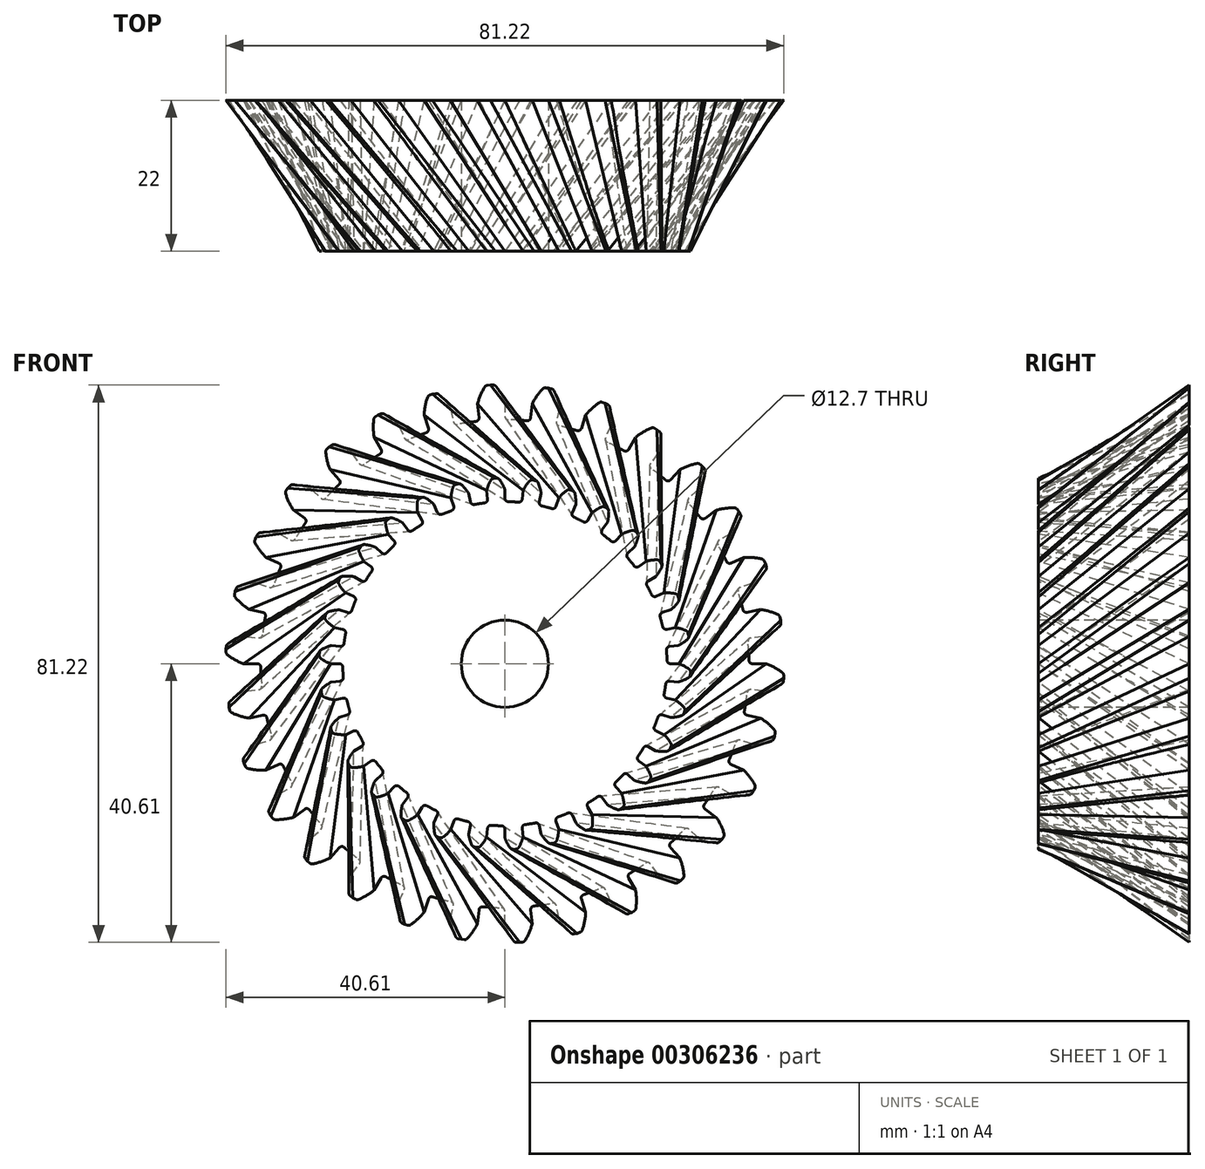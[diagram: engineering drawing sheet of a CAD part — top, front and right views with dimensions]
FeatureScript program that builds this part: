
annotation { "Feature Type Name" : "Feature", "Feature Type Description" : "" }
export const myFeature = defineFeature(function(context is Context, id is Id, definition is map)
    precondition{}
    {
        {
            var Q0;
            Q0=qCreatedBy(makeId("Front.planeOp"),FACE);
            var sketch = newSketch(context, id + "F0", { "sketchPlane" : qUnion([Q0])});
            skArc(sketch, "E0", {"start": v(-4.21, 35.3) * mm, "mid": v(-5.56, 35.12) * mm, "end": v(-6.9, 34.88) * mm});
            skLineSegment(sketch, "E1", {"start": v(0, 0) * mm, "end": v(-3.2, 60.87) * mm, "construction": true});
            skLineSegment(sketch, "E2", {"start": v(-1.69, 40.61) * mm, "end": v(-2.13, 40.61) * mm});
            skLineSegment(sketch, "E3", {"start": v(0, 38.1) * mm, "end": v(0, 36.06) * mm});
            skArc(sketch, "E4.trimOffspring", {"start": v(0, 38.1) * mm, "mid": v(-0.56, 39.3) * mm, "end": v(-1.28, 40.41) * mm});
            skLineSegment(sketch, "E5.MirrorCS", {"start": v(-2.57, 40.57) * mm, "end": v(-2.13, 40.61) * mm});
            skArc(sketch, "E6.MirrorCS", {"start": v(-3.98, 37.9) * mm, "mid": v(-3.55, 39.14) * mm, "end": v(-2.95, 40.32) * mm});
            skLineSegment(sketch, "E7.MirrorCS", {"start": v(-3.98, 37.9) * mm, "end": v(-3.77, 35.87) * mm});
            skPoint(sketch, "E8.orphan", {"position": v(0, 33.66) * mm});
            skPoint(sketch, "E9.orphan", {"position": v(-3.52, 33.47) * mm});
            skPoint(sketch, "E10.visualSharp", {"position": v(-2.81, 40.54) * mm});
            skArc(sketch, "E10.filletArc", {"start": v(-2.57, 40.57) * mm, "mid": v(-2.79, 40.5) * mm, "end": v(-2.95, 40.32) * mm});
            skPoint(sketch, "E11.visualSharp", {"position": v(-1.44, 40.61) * mm});
            skArc(sketch, "E11.filletArc", {"start": v(-1.28, 40.41) * mm, "mid": v(-1.46, 40.56) * mm, "end": v(-1.69, 40.61) * mm});
            skPoint(sketch, "E12.visualSharp", {"position": v(-3.72, 35.37) * mm});
            skArc(sketch, "E12.filletArc", {"start": v(-4.21, 35.3) * mm, "mid": v(-3.88, 35.5) * mm, "end": v(-3.77, 35.87) * mm});
            skPoint(sketch, "E13.visualSharp", {"position": v(0, 35.56) * mm});
            skArc(sketch, "E13.filletArc", {"start": v(0, 36.06) * mm, "mid": v(0.15, 35.7) * mm, "end": v(0.5, 35.56) * mm});
            skArc(sketch, "E14.1.0", {"start": v(-11.46, 33.66) * mm, "mid": v(-11.17, 33.91) * mm, "end": v(-11.14, 34.3) * mm});
            skLineSegment(sketch, "E14.1.1", {"start": v(-11.77, 36.24) * mm, "end": v(-11.14, 34.3) * mm});
            skArc(sketch, "E14.1.2", {"start": v(-11.77, 36.24) * mm, "mid": v(-11.61, 37.55) * mm, "end": v(-11.27, 38.83) * mm});
            skLineSegment(sketch, "E14.1.3", {"start": v(-10.95, 39.15) * mm, "end": v(-10.53, 39.28) * mm});
            skArc(sketch, "E14.1.4", {"start": v(-10.95, 39.15) * mm, "mid": v(-11.14, 39.03) * mm, "end": v(-11.27, 38.83) * mm});
            skLineSegment(sketch, "E14.1.5", {"start": v(-10.1, 39.38) * mm, "end": v(-10.53, 39.28) * mm});
            skArc(sketch, "E14.1.6", {"start": v(-9.66, 39.26) * mm, "mid": v(-9.86, 39.37) * mm, "end": v(-10.1, 39.38) * mm});
            skArc(sketch, "E14.1.7", {"start": v(-7.92, 37.27) * mm, "mid": v(-8.72, 38.33) * mm, "end": v(-9.66, 39.26) * mm});
            skLineSegment(sketch, "E14.1.8", {"start": v(-7.92, 37.27) * mm, "end": v(-7.5, 35.28) * mm});
            skArc(sketch, "E14.1.9", {"start": v(-7.5, 35.28) * mm, "mid": v(-7.28, 34.96) * mm, "end": v(-6.9, 34.88) * mm});
            skArc(sketch, "E14.2.0", {"start": v(-18.21, 30.54) * mm, "mid": v(-17.98, 30.85) * mm, "end": v(-18.03, 31.23) * mm});
            skLineSegment(sketch, "E14.2.1", {"start": v(-19.05, 33) * mm, "end": v(-18.03, 31.23) * mm});
            skArc(sketch, "E14.2.2", {"start": v(-19.05, 33) * mm, "mid": v(-19.16, 34.32) * mm, "end": v(-19.1, 35.64) * mm});
            skLineSegment(sketch, "E14.2.3", {"start": v(-18.85, 36.02) * mm, "end": v(-18.46, 36.24) * mm});
            skArc(sketch, "E14.2.4", {"start": v(-18.85, 36.02) * mm, "mid": v(-19.01, 35.86) * mm, "end": v(-19.1, 35.64) * mm});
            skLineSegment(sketch, "E14.2.5", {"start": v(-18.06, 36.42) * mm, "end": v(-18.46, 36.24) * mm});
            skArc(sketch, "E14.2.6", {"start": v(-17.6, 36.4) * mm, "mid": v(-17.83, 36.46) * mm, "end": v(-18.06, 36.42) * mm});
            skArc(sketch, "E14.2.7", {"start": v(-15.5, 34.8) * mm, "mid": v(-16.5, 35.68) * mm, "end": v(-17.6, 36.4) * mm});
            skLineSegment(sketch, "E14.2.8", {"start": v(-15.5, 34.8) * mm, "end": v(-14.67, 32.95) * mm});
            skArc(sketch, "E14.2.9", {"start": v(-14.67, 32.95) * mm, "mid": v(-14.4, 32.68) * mm, "end": v(-14, 32.69) * mm});
            skArc(sketch, "E14.3.0", {"start": v(-24.16, 26.09) * mm, "mid": v(-24, 26.44) * mm, "end": v(-24.13, 26.8) * mm});
            skLineSegment(sketch, "E14.3.1", {"start": v(-25.5, 28.31) * mm, "end": v(-24.13, 26.8) * mm});
            skArc(sketch, "E14.3.2", {"start": v(-25.5, 28.31) * mm, "mid": v(-25.88, 29.58) * mm, "end": v(-26.09, 30.9) * mm});
            skLineSegment(sketch, "E14.3.3", {"start": v(-25.92, 31.31) * mm, "end": v(-25.6, 31.6) * mm});
            skArc(sketch, "E14.3.4", {"start": v(-25.92, 31.31) * mm, "mid": v(-26.05, 31.12) * mm, "end": v(-26.09, 30.9) * mm});
            skLineSegment(sketch, "E14.3.5", {"start": v(-25.24, 31.87) * mm, "end": v(-25.6, 31.6) * mm});
            skArc(sketch, "E14.3.6", {"start": v(-24.8, 31.94) * mm, "mid": v(-25.02, 31.96) * mm, "end": v(-25.24, 31.87) * mm});
            skArc(sketch, "E14.3.7", {"start": v(-22.4, 30.82) * mm, "mid": v(-23.55, 31.47) * mm, "end": v(-24.8, 31.94) * mm});
            skLineSegment(sketch, "E14.3.8", {"start": v(-22.4, 30.82) * mm, "end": v(-21.2, 29.18) * mm});
            skArc(sketch, "E14.3.9", {"start": v(-21.2, 29.18) * mm, "mid": v(-20.87, 28.97) * mm, "end": v(-20.5, 29.06) * mm});
            skArc(sketch, "E14.4.0", {"start": v(-29.06, 20.5) * mm, "mid": v(-28.97, 20.87) * mm, "end": v(-29.18, 21.2) * mm});
            skLineSegment(sketch, "E14.4.1", {"start": v(-30.82, 22.4) * mm, "end": v(-29.18, 21.2) * mm});
            skArc(sketch, "E14.4.2", {"start": v(-30.82, 22.4) * mm, "mid": v(-31.47, 23.55) * mm, "end": v(-31.94, 24.8) * mm});
            skLineSegment(sketch, "E14.4.3", {"start": v(-31.87, 25.24) * mm, "end": v(-31.6, 25.6) * mm});
            skArc(sketch, "E14.4.4", {"start": v(-31.87, 25.24) * mm, "mid": v(-31.96, 25.02) * mm, "end": v(-31.94, 24.8) * mm});
            skLineSegment(sketch, "E14.4.5", {"start": v(-31.31, 25.92) * mm, "end": v(-31.6, 25.6) * mm});
            skArc(sketch, "E14.4.6", {"start": v(-30.9, 26.09) * mm, "mid": v(-31.12, 26.05) * mm, "end": v(-31.31, 25.92) * mm});
            skArc(sketch, "E14.4.7", {"start": v(-28.31, 25.5) * mm, "mid": v(-29.58, 25.88) * mm, "end": v(-30.9, 26.09) * mm});
            skLineSegment(sketch, "E14.4.8", {"start": v(-28.31, 25.5) * mm, "end": v(-26.8, 24.13) * mm});
            skArc(sketch, "E14.4.9", {"start": v(-26.8, 24.13) * mm, "mid": v(-26.44, 24) * mm, "end": v(-26.09, 24.16) * mm});
            skArc(sketch, "E14.5.0", {"start": v(-32.69, 14) * mm, "mid": v(-32.68, 14.4) * mm, "end": v(-32.95, 14.67) * mm});
            skLineSegment(sketch, "E14.5.1", {"start": v(-34.8, 15.5) * mm, "end": v(-32.95, 14.67) * mm});
            skArc(sketch, "E14.5.2", {"start": v(-34.8, 15.5) * mm, "mid": v(-35.68, 16.5) * mm, "end": v(-36.4, 17.6) * mm});
            skLineSegment(sketch, "E14.5.3", {"start": v(-36.42, 18.06) * mm, "end": v(-36.24, 18.46) * mm});
            skArc(sketch, "E14.5.4", {"start": v(-36.42, 18.06) * mm, "mid": v(-36.46, 17.83) * mm, "end": v(-36.4, 17.6) * mm});
            skLineSegment(sketch, "E14.5.5", {"start": v(-36.02, 18.85) * mm, "end": v(-36.24, 18.46) * mm});
            skArc(sketch, "E14.5.6", {"start": v(-35.64, 19.1) * mm, "mid": v(-35.86, 19.01) * mm, "end": v(-36.02, 18.85) * mm});
            skArc(sketch, "E14.5.7", {"start": v(-33, 19.05) * mm, "mid": v(-34.32, 19.16) * mm, "end": v(-35.64, 19.1) * mm});
            skLineSegment(sketch, "E14.5.8", {"start": v(-33, 19.05) * mm, "end": v(-31.23, 18.03) * mm});
            skArc(sketch, "E14.5.9", {"start": v(-31.23, 18.03) * mm, "mid": v(-30.85, 17.98) * mm, "end": v(-30.54, 18.21) * mm});
            skArc(sketch, "E14.6.0", {"start": v(-34.88, 6.9) * mm, "mid": v(-34.96, 7.28) * mm, "end": v(-35.28, 7.5) * mm});
            skLineSegment(sketch, "E14.6.1", {"start": v(-37.27, 7.92) * mm, "end": v(-35.28, 7.5) * mm});
            skArc(sketch, "E14.6.2", {"start": v(-37.27, 7.92) * mm, "mid": v(-38.33, 8.72) * mm, "end": v(-39.26, 9.66) * mm});
            skLineSegment(sketch, "E14.6.3", {"start": v(-39.38, 10.1) * mm, "end": v(-39.28, 10.53) * mm});
            skArc(sketch, "E14.6.4", {"start": v(-39.38, 10.1) * mm, "mid": v(-39.37, 9.86) * mm, "end": v(-39.26, 9.66) * mm});
            skLineSegment(sketch, "E14.6.5", {"start": v(-39.15, 10.95) * mm, "end": v(-39.28, 10.53) * mm});
            skArc(sketch, "E14.6.6", {"start": v(-38.83, 11.27) * mm, "mid": v(-39.03, 11.14) * mm, "end": v(-39.15, 10.95) * mm});
            skArc(sketch, "E14.6.7", {"start": v(-36.24, 11.77) * mm, "mid": v(-37.55, 11.61) * mm, "end": v(-38.83, 11.27) * mm});
            skLineSegment(sketch, "E14.6.8", {"start": v(-36.24, 11.77) * mm, "end": v(-34.3, 11.14) * mm});
            skArc(sketch, "E14.6.9", {"start": v(-34.3, 11.14) * mm, "mid": v(-33.91, 11.17) * mm, "end": v(-33.66, 11.46) * mm});
            skArc(sketch, "E14.7.0", {"start": v(-35.56, -0.5) * mm, "mid": v(-35.7, -0.15) * mm, "end": v(-36.06, 0) * mm});
            skLineSegment(sketch, "E14.7.1", {"start": v(-38.1, 0) * mm, "end": v(-36.06, 0) * mm});
            skArc(sketch, "E14.7.2", {"start": v(-38.1, 0) * mm, "mid": v(-39.3, 0.56) * mm, "end": v(-40.41, 1.28) * mm});
            skLineSegment(sketch, "E14.7.3", {"start": v(-40.61, 1.69) * mm, "end": v(-40.61, 2.13) * mm});
            skArc(sketch, "E14.7.4", {"start": v(-40.61, 1.69) * mm, "mid": v(-40.56, 1.46) * mm, "end": v(-40.41, 1.28) * mm});
            skLineSegment(sketch, "E14.7.5", {"start": v(-40.57, 2.57) * mm, "end": v(-40.61, 2.13) * mm});
            skArc(sketch, "E14.7.6", {"start": v(-40.32, 2.95) * mm, "mid": v(-40.5, 2.79) * mm, "end": v(-40.57, 2.57) * mm});
            skArc(sketch, "E14.7.7", {"start": v(-37.9, 3.98) * mm, "mid": v(-39.14, 3.55) * mm, "end": v(-40.32, 2.95) * mm});
            skLineSegment(sketch, "E14.7.8", {"start": v(-37.9, 3.98) * mm, "end": v(-35.87, 3.77) * mm});
            skArc(sketch, "E14.7.9", {"start": v(-35.87, 3.77) * mm, "mid": v(-35.5, 3.88) * mm, "end": v(-35.3, 4.21) * mm});
            skArc(sketch, "E14.8.0", {"start": v(-34.68, -7.88) * mm, "mid": v(-34.9, -7.57) * mm, "end": v(-35.28, -7.5) * mm});
            skLineSegment(sketch, "E14.8.1", {"start": v(-37.27, -7.92) * mm, "end": v(-35.28, -7.5) * mm});
            skArc(sketch, "E14.8.2", {"start": v(-37.27, -7.92) * mm, "mid": v(-38.56, -7.62) * mm, "end": v(-39.8, -7.15) * mm});
            skLineSegment(sketch, "E14.8.3", {"start": v(-40.08, -6.8) * mm, "end": v(-40.17, -6.36) * mm});
            skArc(sketch, "E14.8.4", {"start": v(-40.08, -6.8) * mm, "mid": v(-39.98, -7) * mm, "end": v(-39.8, -7.15) * mm});
            skLineSegment(sketch, "E14.8.5", {"start": v(-40.22, -5.92) * mm, "end": v(-40.17, -6.36) * mm});
            skArc(sketch, "E14.8.6", {"start": v(-40.06, -5.5) * mm, "mid": v(-40.19, -5.7) * mm, "end": v(-40.22, -5.92) * mm});
            skArc(sketch, "E14.8.7", {"start": v(-37.9, -3.98) * mm, "mid": v(-39.03, -4.67) * mm, "end": v(-40.06, -5.5) * mm});
            skLineSegment(sketch, "E14.8.8", {"start": v(-37.9, -3.98) * mm, "end": v(-35.87, -3.77) * mm});
            skArc(sketch, "E14.8.9", {"start": v(-35.87, -3.77) * mm, "mid": v(-35.53, -3.59) * mm, "end": v(-35.41, -3.22) * mm});
            skArc(sketch, "E14.9.0", {"start": v(-32.28, -14.92) * mm, "mid": v(-32.56, -14.66) * mm, "end": v(-32.95, -14.67) * mm});
            skLineSegment(sketch, "E14.9.1", {"start": v(-34.8, -15.5) * mm, "end": v(-32.95, -14.67) * mm});
            skArc(sketch, "E14.9.2", {"start": v(-34.8, -15.5) * mm, "mid": v(-36.13, -15.47) * mm, "end": v(-37.44, -15.27) * mm});
            skLineSegment(sketch, "E14.9.3", {"start": v(-37.79, -14.98) * mm, "end": v(-37.97, -14.57) * mm});
            skArc(sketch, "E14.9.4", {"start": v(-37.79, -14.98) * mm, "mid": v(-37.65, -15.16) * mm, "end": v(-37.44, -15.27) * mm});
            skLineSegment(sketch, "E14.9.5", {"start": v(-38.1, -14.16) * mm, "end": v(-37.97, -14.57) * mm});
            skArc(sketch, "E14.9.6", {"start": v(-38.04, -13.7) * mm, "mid": v(-38.12, -13.92) * mm, "end": v(-38.1, -14.16) * mm});
            skArc(sketch, "E14.9.7", {"start": v(-36.24, -11.77) * mm, "mid": v(-37.2, -12.68) * mm, "end": v(-38.04, -13.7) * mm});
            skLineSegment(sketch, "E14.9.8", {"start": v(-36.24, -11.77) * mm, "end": v(-34.3, -11.14) * mm});
            skArc(sketch, "E14.9.9", {"start": v(-34.3, -11.14) * mm, "mid": v(-34, -10.9) * mm, "end": v(-33.97, -10.51) * mm});
            skArc(sketch, "E14.10.0", {"start": v(-28.47, -21.3) * mm, "mid": v(-28.8, -21.1) * mm, "end": v(-29.18, -21.2) * mm});
            skLineSegment(sketch, "E14.10.1", {"start": v(-30.82, -22.4) * mm, "end": v(-29.18, -21.2) * mm});
            skArc(sketch, "E14.10.2", {"start": v(-30.82, -22.4) * mm, "mid": v(-32.12, -22.65) * mm, "end": v(-33.45, -22.72) * mm});
            skLineSegment(sketch, "E14.10.3", {"start": v(-33.85, -22.5) * mm, "end": v(-34.1, -22.15) * mm});
            skArc(sketch, "E14.10.4", {"start": v(-33.85, -22.5) * mm, "mid": v(-33.67, -22.66) * mm, "end": v(-33.45, -22.72) * mm});
            skLineSegment(sketch, "E14.10.5", {"start": v(-34.33, -21.77) * mm, "end": v(-34.1, -22.15) * mm});
            skArc(sketch, "E14.10.6", {"start": v(-34.36, -21.32) * mm, "mid": v(-34.4, -21.55) * mm, "end": v(-34.33, -21.77) * mm});
            skArc(sketch, "E14.10.7", {"start": v(-33, -19.05) * mm, "mid": v(-33.76, -20.14) * mm, "end": v(-34.36, -21.32) * mm});
            skLineSegment(sketch, "E14.10.8", {"start": v(-33, -19.05) * mm, "end": v(-31.23, -18.03) * mm});
            skArc(sketch, "E14.10.9", {"start": v(-31.23, -18.03) * mm, "mid": v(-31, -17.73) * mm, "end": v(-31.04, -17.34) * mm});
            skArc(sketch, "E14.11.0", {"start": v(-23.42, -26.76) * mm, "mid": v(-23.78, -26.63) * mm, "end": v(-24.13, -26.8) * mm});
            skLineSegment(sketch, "E14.11.1", {"start": v(-25.5, -28.31) * mm, "end": v(-24.13, -26.8) * mm});
            skArc(sketch, "E14.11.2", {"start": v(-25.5, -28.31) * mm, "mid": v(-26.71, -28.83) * mm, "end": v(-28, -29.17) * mm});
            skLineSegment(sketch, "E14.11.3", {"start": v(-28.43, -29.05) * mm, "end": v(-28.76, -28.76) * mm});
            skArc(sketch, "E14.11.4", {"start": v(-28.43, -29.05) * mm, "mid": v(-28.23, -29.16) * mm, "end": v(-28, -29.17) * mm});
            skLineSegment(sketch, "E14.11.5", {"start": v(-29.05, -28.43) * mm, "end": v(-28.76, -28.76) * mm});
            skArc(sketch, "E14.11.6", {"start": v(-29.17, -28) * mm, "mid": v(-29.16, -28.23) * mm, "end": v(-29.05, -28.43) * mm});
            skArc(sketch, "E14.11.7", {"start": v(-28.31, -25.5) * mm, "mid": v(-28.83, -26.71) * mm, "end": v(-29.17, -28) * mm});
            skLineSegment(sketch, "E14.11.8", {"start": v(-28.31, -25.5) * mm, "end": v(-26.8, -24.13) * mm});
            skArc(sketch, "E14.11.9", {"start": v(-26.8, -24.13) * mm, "mid": v(-26.63, -23.78) * mm, "end": v(-26.76, -23.42) * mm});
            skArc(sketch, "E14.12.0", {"start": v(-17.34, -31.04) * mm, "mid": v(-17.73, -31) * mm, "end": v(-18.03, -31.23) * mm});
            skLineSegment(sketch, "E14.12.1", {"start": v(-19.05, -33) * mm, "end": v(-18.03, -31.23) * mm});
            skArc(sketch, "E14.12.2", {"start": v(-19.05, -33) * mm, "mid": v(-20.14, -33.76) * mm, "end": v(-21.32, -34.36) * mm});
            skLineSegment(sketch, "E14.12.3", {"start": v(-21.77, -34.33) * mm, "end": v(-22.15, -34.1) * mm});
            skArc(sketch, "E14.12.4", {"start": v(-21.77, -34.33) * mm, "mid": v(-21.55, -34.4) * mm, "end": v(-21.32, -34.36) * mm});
            skLineSegment(sketch, "E14.12.5", {"start": v(-22.5, -33.85) * mm, "end": v(-22.15, -34.1) * mm});
            skArc(sketch, "E14.12.6", {"start": v(-22.72, -33.45) * mm, "mid": v(-22.66, -33.67) * mm, "end": v(-22.5, -33.85) * mm});
            skArc(sketch, "E14.12.7", {"start": v(-22.4, -30.82) * mm, "mid": v(-22.65, -32.12) * mm, "end": v(-22.72, -33.45) * mm});
            skLineSegment(sketch, "E14.12.8", {"start": v(-22.4, -30.82) * mm, "end": v(-21.2, -29.18) * mm});
            skArc(sketch, "E14.12.9", {"start": v(-21.2, -29.18) * mm, "mid": v(-21.1, -28.8) * mm, "end": v(-21.3, -28.47) * mm});
            skArc(sketch, "E14.13.0", {"start": v(-10.51, -33.97) * mm, "mid": v(-10.9, -34) * mm, "end": v(-11.14, -34.3) * mm});
            skLineSegment(sketch, "E14.13.1", {"start": v(-11.77, -36.24) * mm, "end": v(-11.14, -34.3) * mm});
            skArc(sketch, "E14.13.2", {"start": v(-11.77, -36.24) * mm, "mid": v(-12.68, -37.2) * mm, "end": v(-13.7, -38.04) * mm});
            skLineSegment(sketch, "E14.13.3", {"start": v(-14.16, -38.1) * mm, "end": v(-14.57, -37.97) * mm});
            skArc(sketch, "E14.13.4", {"start": v(-14.16, -38.1) * mm, "mid": v(-13.92, -38.12) * mm, "end": v(-13.7, -38.04) * mm});
            skLineSegment(sketch, "E14.13.5", {"start": v(-14.98, -37.79) * mm, "end": v(-14.57, -37.97) * mm});
            skArc(sketch, "E14.13.6", {"start": v(-15.27, -37.44) * mm, "mid": v(-15.16, -37.65) * mm, "end": v(-14.98, -37.79) * mm});
            skArc(sketch, "E14.13.7", {"start": v(-15.5, -34.8) * mm, "mid": v(-15.47, -36.13) * mm, "end": v(-15.27, -37.44) * mm});
            skLineSegment(sketch, "E14.13.8", {"start": v(-15.5, -34.8) * mm, "end": v(-14.67, -32.95) * mm});
            skArc(sketch, "E14.13.9", {"start": v(-14.67, -32.95) * mm, "mid": v(-14.66, -32.56) * mm, "end": v(-14.92, -32.28) * mm});
            skArc(sketch, "E14.14.0", {"start": v(-3.22, -35.41) * mm, "mid": v(-3.59, -35.53) * mm, "end": v(-3.77, -35.87) * mm});
            skLineSegment(sketch, "E14.14.1", {"start": v(-3.98, -37.9) * mm, "end": v(-3.77, -35.87) * mm});
            skArc(sketch, "E14.14.2", {"start": v(-3.98, -37.9) * mm, "mid": v(-4.67, -39.03) * mm, "end": v(-5.5, -40.06) * mm});
            skLineSegment(sketch, "E14.14.3", {"start": v(-5.92, -40.22) * mm, "end": v(-6.36, -40.17) * mm});
            skArc(sketch, "E14.14.4", {"start": v(-5.92, -40.22) * mm, "mid": v(-5.7, -40.19) * mm, "end": v(-5.5, -40.06) * mm});
            skLineSegment(sketch, "E14.14.5", {"start": v(-6.8, -40.08) * mm, "end": v(-6.36, -40.17) * mm});
            skArc(sketch, "E14.14.6", {"start": v(-7.15, -39.8) * mm, "mid": v(-7, -39.98) * mm, "end": v(-6.8, -40.08) * mm});
            skArc(sketch, "E14.14.7", {"start": v(-7.92, -37.27) * mm, "mid": v(-7.62, -38.56) * mm, "end": v(-7.15, -39.8) * mm});
            skLineSegment(sketch, "E14.14.8", {"start": v(-7.92, -37.27) * mm, "end": v(-7.5, -35.28) * mm});
            skArc(sketch, "E14.14.9", {"start": v(-7.5, -35.28) * mm, "mid": v(-7.57, -34.9) * mm, "end": v(-7.88, -34.68) * mm});
            skArc(sketch, "E14.15.0", {"start": v(4.21, -35.3) * mm, "mid": v(3.88, -35.5) * mm, "end": v(3.77, -35.87) * mm});
            skLineSegment(sketch, "E14.15.1", {"start": v(3.98, -37.9) * mm, "end": v(3.77, -35.87) * mm});
            skArc(sketch, "E14.15.2", {"start": v(3.98, -37.9) * mm, "mid": v(3.55, -39.14) * mm, "end": v(2.95, -40.32) * mm});
            skLineSegment(sketch, "E14.15.3", {"start": v(2.57, -40.57) * mm, "end": v(2.13, -40.61) * mm});
            skArc(sketch, "E14.15.4", {"start": v(2.57, -40.57) * mm, "mid": v(2.79, -40.5) * mm, "end": v(2.95, -40.32) * mm});
            skLineSegment(sketch, "E14.15.5", {"start": v(1.69, -40.61) * mm, "end": v(2.13, -40.61) * mm});
            skArc(sketch, "E14.15.6", {"start": v(1.28, -40.41) * mm, "mid": v(1.46, -40.56) * mm, "end": v(1.69, -40.61) * mm});
            skArc(sketch, "E14.15.7", {"start": v(0, -38.1) * mm, "mid": v(0.56, -39.3) * mm, "end": v(1.28, -40.41) * mm});
            skLineSegment(sketch, "E14.15.8", {"start": v(0, -38.1) * mm, "end": v(0, -36.06) * mm});
            skArc(sketch, "E14.15.9", {"start": v(0, -36.06) * mm, "mid": v(-0.15, -35.7) * mm, "end": v(-0.5, -35.56) * mm});
            skArc(sketch, "E14.16.0", {"start": v(11.46, -33.66) * mm, "mid": v(11.17, -33.91) * mm, "end": v(11.14, -34.3) * mm});
            skLineSegment(sketch, "E14.16.1", {"start": v(11.77, -36.24) * mm, "end": v(11.14, -34.3) * mm});
            skArc(sketch, "E14.16.2", {"start": v(11.77, -36.24) * mm, "mid": v(11.61, -37.55) * mm, "end": v(11.27, -38.83) * mm});
            skLineSegment(sketch, "E14.16.3", {"start": v(10.95, -39.15) * mm, "end": v(10.53, -39.28) * mm});
            skArc(sketch, "E14.16.4", {"start": v(10.95, -39.15) * mm, "mid": v(11.14, -39.03) * mm, "end": v(11.27, -38.83) * mm});
            skLineSegment(sketch, "E14.16.5", {"start": v(10.1, -39.38) * mm, "end": v(10.53, -39.28) * mm});
            skArc(sketch, "E14.16.6", {"start": v(9.66, -39.26) * mm, "mid": v(9.86, -39.37) * mm, "end": v(10.1, -39.38) * mm});
            skArc(sketch, "E14.16.7", {"start": v(7.92, -37.27) * mm, "mid": v(8.72, -38.33) * mm, "end": v(9.66, -39.26) * mm});
            skLineSegment(sketch, "E14.16.8", {"start": v(7.92, -37.27) * mm, "end": v(7.5, -35.28) * mm});
            skArc(sketch, "E14.16.9", {"start": v(7.5, -35.28) * mm, "mid": v(7.28, -34.96) * mm, "end": v(6.9, -34.88) * mm});
            skArc(sketch, "E14.17.0", {"start": v(18.21, -30.54) * mm, "mid": v(17.98, -30.85) * mm, "end": v(18.03, -31.23) * mm});
            skLineSegment(sketch, "E14.17.1", {"start": v(19.05, -33) * mm, "end": v(18.03, -31.23) * mm});
            skArc(sketch, "E14.17.2", {"start": v(19.05, -33) * mm, "mid": v(19.16, -34.32) * mm, "end": v(19.1, -35.64) * mm});
            skLineSegment(sketch, "E14.17.3", {"start": v(18.85, -36.02) * mm, "end": v(18.46, -36.24) * mm});
            skArc(sketch, "E14.17.4", {"start": v(18.85, -36.02) * mm, "mid": v(19.01, -35.86) * mm, "end": v(19.1, -35.64) * mm});
            skLineSegment(sketch, "E14.17.5", {"start": v(18.06, -36.42) * mm, "end": v(18.46, -36.24) * mm});
            skArc(sketch, "E14.17.6", {"start": v(17.6, -36.4) * mm, "mid": v(17.83, -36.46) * mm, "end": v(18.06, -36.42) * mm});
            skArc(sketch, "E14.17.7", {"start": v(15.5, -34.8) * mm, "mid": v(16.5, -35.68) * mm, "end": v(17.6, -36.4) * mm});
            skLineSegment(sketch, "E14.17.8", {"start": v(15.5, -34.8) * mm, "end": v(14.67, -32.95) * mm});
            skArc(sketch, "E14.17.9", {"start": v(14.67, -32.95) * mm, "mid": v(14.4, -32.68) * mm, "end": v(14, -32.69) * mm});
            skArc(sketch, "E14.18.0", {"start": v(24.16, -26.09) * mm, "mid": v(24, -26.44) * mm, "end": v(24.13, -26.8) * mm});
            skLineSegment(sketch, "E14.18.1", {"start": v(25.5, -28.31) * mm, "end": v(24.13, -26.8) * mm});
            skArc(sketch, "E14.18.2", {"start": v(25.5, -28.31) * mm, "mid": v(25.88, -29.58) * mm, "end": v(26.09, -30.9) * mm});
            skLineSegment(sketch, "E14.18.3", {"start": v(25.92, -31.31) * mm, "end": v(25.6, -31.6) * mm});
            skArc(sketch, "E14.18.4", {"start": v(25.92, -31.31) * mm, "mid": v(26.05, -31.12) * mm, "end": v(26.09, -30.9) * mm});
            skLineSegment(sketch, "E14.18.5", {"start": v(25.24, -31.87) * mm, "end": v(25.6, -31.6) * mm});
            skArc(sketch, "E14.18.6", {"start": v(24.8, -31.94) * mm, "mid": v(25.02, -31.96) * mm, "end": v(25.24, -31.87) * mm});
            skArc(sketch, "E14.18.7", {"start": v(22.4, -30.82) * mm, "mid": v(23.55, -31.47) * mm, "end": v(24.8, -31.94) * mm});
            skLineSegment(sketch, "E14.18.8", {"start": v(22.4, -30.82) * mm, "end": v(21.2, -29.18) * mm});
            skArc(sketch, "E14.18.9", {"start": v(21.2, -29.18) * mm, "mid": v(20.87, -28.97) * mm, "end": v(20.5, -29.06) * mm});
            skArc(sketch, "E14.19.0", {"start": v(29.06, -20.5) * mm, "mid": v(28.97, -20.87) * mm, "end": v(29.18, -21.2) * mm});
            skLineSegment(sketch, "E14.19.1", {"start": v(30.82, -22.4) * mm, "end": v(29.18, -21.2) * mm});
            skArc(sketch, "E14.19.2", {"start": v(30.82, -22.4) * mm, "mid": v(31.47, -23.55) * mm, "end": v(31.94, -24.8) * mm});
            skLineSegment(sketch, "E14.19.3", {"start": v(31.87, -25.24) * mm, "end": v(31.6, -25.6) * mm});
            skArc(sketch, "E14.19.4", {"start": v(31.87, -25.24) * mm, "mid": v(31.96, -25.02) * mm, "end": v(31.94, -24.8) * mm});
            skLineSegment(sketch, "E14.19.5", {"start": v(31.31, -25.92) * mm, "end": v(31.6, -25.6) * mm});
            skArc(sketch, "E14.19.6", {"start": v(30.9, -26.09) * mm, "mid": v(31.12, -26.05) * mm, "end": v(31.31, -25.92) * mm});
            skArc(sketch, "E14.19.7", {"start": v(28.31, -25.5) * mm, "mid": v(29.58, -25.88) * mm, "end": v(30.9, -26.09) * mm});
            skLineSegment(sketch, "E14.19.8", {"start": v(28.31, -25.5) * mm, "end": v(26.8, -24.13) * mm});
            skArc(sketch, "E14.19.9", {"start": v(26.8, -24.13) * mm, "mid": v(26.44, -24) * mm, "end": v(26.09, -24.16) * mm});
            skArc(sketch, "E14.20.0", {"start": v(32.69, -14) * mm, "mid": v(32.68, -14.4) * mm, "end": v(32.95, -14.67) * mm});
            skLineSegment(sketch, "E14.20.1", {"start": v(34.8, -15.5) * mm, "end": v(32.95, -14.67) * mm});
            skArc(sketch, "E14.20.2", {"start": v(34.8, -15.5) * mm, "mid": v(35.68, -16.5) * mm, "end": v(36.4, -17.6) * mm});
            skLineSegment(sketch, "E14.20.3", {"start": v(36.42, -18.06) * mm, "end": v(36.24, -18.46) * mm});
            skArc(sketch, "E14.20.4", {"start": v(36.42, -18.06) * mm, "mid": v(36.46, -17.83) * mm, "end": v(36.4, -17.6) * mm});
            skLineSegment(sketch, "E14.20.5", {"start": v(36.02, -18.85) * mm, "end": v(36.24, -18.46) * mm});
            skArc(sketch, "E14.20.6", {"start": v(35.64, -19.1) * mm, "mid": v(35.86, -19.01) * mm, "end": v(36.02, -18.85) * mm});
            skArc(sketch, "E14.20.7", {"start": v(33, -19.05) * mm, "mid": v(34.32, -19.16) * mm, "end": v(35.64, -19.1) * mm});
            skLineSegment(sketch, "E14.20.8", {"start": v(33, -19.05) * mm, "end": v(31.23, -18.03) * mm});
            skArc(sketch, "E14.20.9", {"start": v(31.23, -18.03) * mm, "mid": v(30.85, -17.98) * mm, "end": v(30.54, -18.21) * mm});
            skArc(sketch, "E14.21.0", {"start": v(34.88, -6.9) * mm, "mid": v(34.96, -7.28) * mm, "end": v(35.28, -7.5) * mm});
            skLineSegment(sketch, "E14.21.1", {"start": v(37.27, -7.92) * mm, "end": v(35.28, -7.5) * mm});
            skArc(sketch, "E14.21.2", {"start": v(37.27, -7.92) * mm, "mid": v(38.33, -8.72) * mm, "end": v(39.26, -9.66) * mm});
            skLineSegment(sketch, "E14.21.3", {"start": v(39.38, -10.1) * mm, "end": v(39.28, -10.53) * mm});
            skArc(sketch, "E14.21.4", {"start": v(39.38, -10.1) * mm, "mid": v(39.37, -9.86) * mm, "end": v(39.26, -9.66) * mm});
            skLineSegment(sketch, "E14.21.5", {"start": v(39.15, -10.95) * mm, "end": v(39.28, -10.53) * mm});
            skArc(sketch, "E14.21.6", {"start": v(38.83, -11.27) * mm, "mid": v(39.03, -11.14) * mm, "end": v(39.15, -10.95) * mm});
            skArc(sketch, "E14.21.7", {"start": v(36.24, -11.77) * mm, "mid": v(37.55, -11.61) * mm, "end": v(38.83, -11.27) * mm});
            skLineSegment(sketch, "E14.21.8", {"start": v(36.24, -11.77) * mm, "end": v(34.3, -11.14) * mm});
            skArc(sketch, "E14.21.9", {"start": v(34.3, -11.14) * mm, "mid": v(33.91, -11.17) * mm, "end": v(33.66, -11.46) * mm});
            skArc(sketch, "E14.22.0", {"start": v(35.56, 0.5) * mm, "mid": v(35.7, 0.15) * mm, "end": v(36.06, 0) * mm});
            skLineSegment(sketch, "E14.22.1", {"start": v(38.1, 0) * mm, "end": v(36.06, 0) * mm});
            skArc(sketch, "E14.22.2", {"start": v(38.1, 0) * mm, "mid": v(39.3, -0.56) * mm, "end": v(40.41, -1.28) * mm});
            skLineSegment(sketch, "E14.22.3", {"start": v(40.61, -1.69) * mm, "end": v(40.61, -2.13) * mm});
            skArc(sketch, "E14.22.4", {"start": v(40.61, -1.69) * mm, "mid": v(40.56, -1.46) * mm, "end": v(40.41, -1.28) * mm});
            skLineSegment(sketch, "E14.22.5", {"start": v(40.57, -2.57) * mm, "end": v(40.61, -2.13) * mm});
            skArc(sketch, "E14.22.6", {"start": v(40.32, -2.95) * mm, "mid": v(40.5, -2.79) * mm, "end": v(40.57, -2.57) * mm});
            skArc(sketch, "E14.22.7", {"start": v(37.9, -3.98) * mm, "mid": v(39.14, -3.55) * mm, "end": v(40.32, -2.95) * mm});
            skLineSegment(sketch, "E14.22.8", {"start": v(37.9, -3.98) * mm, "end": v(35.87, -3.77) * mm});
            skArc(sketch, "E14.22.9", {"start": v(35.87, -3.77) * mm, "mid": v(35.5, -3.88) * mm, "end": v(35.3, -4.21) * mm});
            skArc(sketch, "E14.23.0", {"start": v(34.68, 7.88) * mm, "mid": v(34.9, 7.57) * mm, "end": v(35.28, 7.5) * mm});
            skLineSegment(sketch, "E14.23.1", {"start": v(37.27, 7.92) * mm, "end": v(35.28, 7.5) * mm});
            skArc(sketch, "E14.23.2", {"start": v(37.27, 7.92) * mm, "mid": v(38.56, 7.62) * mm, "end": v(39.8, 7.15) * mm});
            skLineSegment(sketch, "E14.23.3", {"start": v(40.08, 6.8) * mm, "end": v(40.17, 6.36) * mm});
            skArc(sketch, "E14.23.4", {"start": v(40.08, 6.8) * mm, "mid": v(39.98, 7) * mm, "end": v(39.8, 7.15) * mm});
            skLineSegment(sketch, "E14.23.5", {"start": v(40.22, 5.92) * mm, "end": v(40.17, 6.36) * mm});
            skArc(sketch, "E14.23.6", {"start": v(40.06, 5.5) * mm, "mid": v(40.19, 5.7) * mm, "end": v(40.22, 5.92) * mm});
            skArc(sketch, "E14.23.7", {"start": v(37.9, 3.98) * mm, "mid": v(39.03, 4.67) * mm, "end": v(40.06, 5.5) * mm});
            skLineSegment(sketch, "E14.23.8", {"start": v(37.9, 3.98) * mm, "end": v(35.87, 3.77) * mm});
            skArc(sketch, "E14.23.9", {"start": v(35.87, 3.77) * mm, "mid": v(35.53, 3.59) * mm, "end": v(35.41, 3.22) * mm});
            skArc(sketch, "E14.24.0", {"start": v(32.28, 14.92) * mm, "mid": v(32.56, 14.66) * mm, "end": v(32.95, 14.67) * mm});
            skLineSegment(sketch, "E14.24.1", {"start": v(34.8, 15.5) * mm, "end": v(32.95, 14.67) * mm});
            skArc(sketch, "E14.24.2", {"start": v(34.8, 15.5) * mm, "mid": v(36.13, 15.47) * mm, "end": v(37.44, 15.27) * mm});
            skLineSegment(sketch, "E14.24.3", {"start": v(37.79, 14.98) * mm, "end": v(37.97, 14.57) * mm});
            skArc(sketch, "E14.24.4", {"start": v(37.79, 14.98) * mm, "mid": v(37.65, 15.16) * mm, "end": v(37.44, 15.27) * mm});
            skLineSegment(sketch, "E14.24.5", {"start": v(38.1, 14.16) * mm, "end": v(37.97, 14.57) * mm});
            skArc(sketch, "E14.24.6", {"start": v(38.04, 13.7) * mm, "mid": v(38.12, 13.92) * mm, "end": v(38.1, 14.16) * mm});
            skArc(sketch, "E14.24.7", {"start": v(36.24, 11.77) * mm, "mid": v(37.2, 12.68) * mm, "end": v(38.04, 13.7) * mm});
            skLineSegment(sketch, "E14.24.8", {"start": v(36.24, 11.77) * mm, "end": v(34.3, 11.14) * mm});
            skArc(sketch, "E14.24.9", {"start": v(34.3, 11.14) * mm, "mid": v(34, 10.9) * mm, "end": v(33.97, 10.51) * mm});
            skArc(sketch, "E14.25.0", {"start": v(28.47, 21.3) * mm, "mid": v(28.8, 21.1) * mm, "end": v(29.18, 21.2) * mm});
            skLineSegment(sketch, "E14.25.1", {"start": v(30.82, 22.4) * mm, "end": v(29.18, 21.2) * mm});
            skArc(sketch, "E14.25.2", {"start": v(30.82, 22.4) * mm, "mid": v(32.12, 22.65) * mm, "end": v(33.45, 22.72) * mm});
            skLineSegment(sketch, "E14.25.3", {"start": v(33.85, 22.5) * mm, "end": v(34.1, 22.15) * mm});
            skArc(sketch, "E14.25.4", {"start": v(33.85, 22.5) * mm, "mid": v(33.67, 22.66) * mm, "end": v(33.45, 22.72) * mm});
            skLineSegment(sketch, "E14.25.5", {"start": v(34.33, 21.77) * mm, "end": v(34.1, 22.15) * mm});
            skArc(sketch, "E14.25.6", {"start": v(34.36, 21.32) * mm, "mid": v(34.4, 21.55) * mm, "end": v(34.33, 21.77) * mm});
            skArc(sketch, "E14.25.7", {"start": v(33, 19.05) * mm, "mid": v(33.76, 20.14) * mm, "end": v(34.36, 21.32) * mm});
            skLineSegment(sketch, "E14.25.8", {"start": v(33, 19.05) * mm, "end": v(31.23, 18.03) * mm});
            skArc(sketch, "E14.25.9", {"start": v(31.23, 18.03) * mm, "mid": v(31, 17.73) * mm, "end": v(31.04, 17.34) * mm});
            skArc(sketch, "E14.26.0", {"start": v(23.42, 26.76) * mm, "mid": v(23.78, 26.63) * mm, "end": v(24.13, 26.8) * mm});
            skLineSegment(sketch, "E14.26.1", {"start": v(25.5, 28.31) * mm, "end": v(24.13, 26.8) * mm});
            skArc(sketch, "E14.26.2", {"start": v(25.5, 28.31) * mm, "mid": v(26.71, 28.83) * mm, "end": v(28, 29.17) * mm});
            skLineSegment(sketch, "E14.26.3", {"start": v(28.43, 29.05) * mm, "end": v(28.76, 28.76) * mm});
            skArc(sketch, "E14.26.4", {"start": v(28.43, 29.05) * mm, "mid": v(28.23, 29.16) * mm, "end": v(28, 29.17) * mm});
            skLineSegment(sketch, "E14.26.5", {"start": v(29.05, 28.43) * mm, "end": v(28.76, 28.76) * mm});
            skArc(sketch, "E14.26.6", {"start": v(29.17, 28) * mm, "mid": v(29.16, 28.23) * mm, "end": v(29.05, 28.43) * mm});
            skArc(sketch, "E14.26.7", {"start": v(28.31, 25.5) * mm, "mid": v(28.83, 26.71) * mm, "end": v(29.17, 28) * mm});
            skLineSegment(sketch, "E14.26.8", {"start": v(28.31, 25.5) * mm, "end": v(26.8, 24.13) * mm});
            skArc(sketch, "E14.26.9", {"start": v(26.8, 24.13) * mm, "mid": v(26.63, 23.78) * mm, "end": v(26.76, 23.42) * mm});
            skArc(sketch, "E14.27.0", {"start": v(17.34, 31.04) * mm, "mid": v(17.73, 31) * mm, "end": v(18.03, 31.23) * mm});
            skLineSegment(sketch, "E14.27.1", {"start": v(19.05, 33) * mm, "end": v(18.03, 31.23) * mm});
            skArc(sketch, "E14.27.2", {"start": v(19.05, 33) * mm, "mid": v(20.14, 33.76) * mm, "end": v(21.32, 34.36) * mm});
            skLineSegment(sketch, "E14.27.3", {"start": v(21.77, 34.33) * mm, "end": v(22.15, 34.1) * mm});
            skArc(sketch, "E14.27.4", {"start": v(21.77, 34.33) * mm, "mid": v(21.55, 34.4) * mm, "end": v(21.32, 34.36) * mm});
            skLineSegment(sketch, "E14.27.5", {"start": v(22.5, 33.85) * mm, "end": v(22.15, 34.1) * mm});
            skArc(sketch, "E14.27.6", {"start": v(22.72, 33.45) * mm, "mid": v(22.66, 33.67) * mm, "end": v(22.5, 33.85) * mm});
            skArc(sketch, "E14.27.7", {"start": v(22.4, 30.82) * mm, "mid": v(22.65, 32.12) * mm, "end": v(22.72, 33.45) * mm});
            skLineSegment(sketch, "E14.27.8", {"start": v(22.4, 30.82) * mm, "end": v(21.2, 29.18) * mm});
            skArc(sketch, "E14.27.9", {"start": v(21.2, 29.18) * mm, "mid": v(21.1, 28.8) * mm, "end": v(21.3, 28.47) * mm});
            skArc(sketch, "E14.28.0", {"start": v(10.51, 33.97) * mm, "mid": v(10.9, 34) * mm, "end": v(11.14, 34.3) * mm});
            skLineSegment(sketch, "E14.28.1", {"start": v(11.77, 36.24) * mm, "end": v(11.14, 34.3) * mm});
            skArc(sketch, "E14.28.2", {"start": v(11.77, 36.24) * mm, "mid": v(12.68, 37.2) * mm, "end": v(13.7, 38.04) * mm});
            skLineSegment(sketch, "E14.28.3", {"start": v(14.16, 38.1) * mm, "end": v(14.57, 37.97) * mm});
            skArc(sketch, "E14.28.4", {"start": v(14.16, 38.1) * mm, "mid": v(13.92, 38.12) * mm, "end": v(13.7, 38.04) * mm});
            skLineSegment(sketch, "E14.28.5", {"start": v(14.98, 37.79) * mm, "end": v(14.57, 37.97) * mm});
            skArc(sketch, "E14.28.6", {"start": v(15.27, 37.44) * mm, "mid": v(15.16, 37.65) * mm, "end": v(14.98, 37.79) * mm});
            skArc(sketch, "E14.28.7", {"start": v(15.5, 34.8) * mm, "mid": v(15.47, 36.13) * mm, "end": v(15.27, 37.44) * mm});
            skLineSegment(sketch, "E14.28.8", {"start": v(15.5, 34.8) * mm, "end": v(14.67, 32.95) * mm});
            skArc(sketch, "E14.28.9", {"start": v(14.67, 32.95) * mm, "mid": v(14.66, 32.56) * mm, "end": v(14.92, 32.28) * mm});
            skArc(sketch, "E14.29.0", {"start": v(3.22, 35.41) * mm, "mid": v(3.59, 35.53) * mm, "end": v(3.77, 35.87) * mm});
            skLineSegment(sketch, "E14.29.1", {"start": v(3.98, 37.9) * mm, "end": v(3.77, 35.87) * mm});
            skArc(sketch, "E14.29.2", {"start": v(3.98, 37.9) * mm, "mid": v(4.67, 39.03) * mm, "end": v(5.5, 40.06) * mm});
            skLineSegment(sketch, "E14.29.3", {"start": v(5.92, 40.22) * mm, "end": v(6.36, 40.17) * mm});
            skArc(sketch, "E14.29.4", {"start": v(5.92, 40.22) * mm, "mid": v(5.7, 40.19) * mm, "end": v(5.5, 40.06) * mm});
            skLineSegment(sketch, "E14.29.5", {"start": v(6.8, 40.08) * mm, "end": v(6.36, 40.17) * mm});
            skArc(sketch, "E14.29.6", {"start": v(7.15, 39.8) * mm, "mid": v(7, 39.98) * mm, "end": v(6.8, 40.08) * mm});
            skArc(sketch, "E14.29.7", {"start": v(7.92, 37.27) * mm, "mid": v(7.62, 38.56) * mm, "end": v(7.15, 39.8) * mm});
            skLineSegment(sketch, "E14.29.8", {"start": v(7.92, 37.27) * mm, "end": v(7.5, 35.28) * mm});
            skArc(sketch, "E14.29.9", {"start": v(7.5, 35.28) * mm, "mid": v(7.57, 34.9) * mm, "end": v(7.88, 34.68) * mm});
            skArc(sketch, "E15.trimOffspring", {"start": v(-11.46, 33.66) * mm, "mid": v(-12.74, 33.2) * mm, "end": v(-14, 32.69) * mm});
            skArc(sketch, "E16.trimOffspring", {"start": v(-18.21, 30.54) * mm, "mid": v(-19.37, 29.82) * mm, "end": v(-20.5, 29.06) * mm});
            skArc(sketch, "E17.trimOffspring", {"start": v(-24.16, 26.09) * mm, "mid": v(-25.14, 25.14) * mm, "end": v(-26.09, 24.16) * mm});
            skArc(sketch, "E18.trimOffspring", {"start": v(-29.06, 20.5) * mm, "mid": v(-29.82, 19.37) * mm, "end": v(-30.54, 18.21) * mm});
            skArc(sketch, "E19.trimOffspring", {"start": v(-32.69, 14) * mm, "mid": v(-33.2, 12.74) * mm, "end": v(-33.66, 11.46) * mm});
            skArc(sketch, "E20.trimOffspring", {"start": v(-34.88, 6.9) * mm, "mid": v(-35.12, 5.56) * mm, "end": v(-35.3, 4.21) * mm});
            skArc(sketch, "E21.trimOffspring", {"start": v(-35.56, -0.5) * mm, "mid": v(-35.51, -1.86) * mm, "end": v(-35.41, -3.22) * mm});
            skArc(sketch, "E22.trimOffspring", {"start": v(3.22, 35.41) * mm, "mid": v(1.86, 35.51) * mm, "end": v(0.5, 35.56) * mm});
            skArc(sketch, "E23.trimOffspring", {"start": v(10.51, 33.97) * mm, "mid": v(9.2, 34.35) * mm, "end": v(7.88, 34.68) * mm});
            skArc(sketch, "E24.trimOffspring", {"start": v(17.34, 31.04) * mm, "mid": v(16.14, 31.68) * mm, "end": v(14.92, 32.28) * mm});
            skArc(sketch, "E25.trimOffspring", {"start": v(23.42, 26.76) * mm, "mid": v(22.38, 27.64) * mm, "end": v(21.3, 28.47) * mm});
            skArc(sketch, "E26.trimOffspring", {"start": v(28.47, 21.3) * mm, "mid": v(27.64, 22.38) * mm, "end": v(26.76, 23.42) * mm});
            skArc(sketch, "E27.trimOffspring", {"start": v(32.28, 14.92) * mm, "mid": v(31.68, 16.14) * mm, "end": v(31.04, 17.34) * mm});
            skArc(sketch, "E28.trimOffspring", {"start": v(34.68, 7.88) * mm, "mid": v(34.35, 9.2) * mm, "end": v(33.97, 10.51) * mm});
            skArc(sketch, "E29.trimOffspring", {"start": v(35.56, 0.5) * mm, "mid": v(35.51, 1.86) * mm, "end": v(35.41, 3.22) * mm});
            skArc(sketch, "E30.trimOffspring", {"start": v(34.88, -6.9) * mm, "mid": v(35.12, -5.56) * mm, "end": v(35.3, -4.21) * mm});
            skArc(sketch, "E31.trimOffspring", {"start": v(32.69, -14) * mm, "mid": v(33.2, -12.74) * mm, "end": v(33.66, -11.46) * mm});
            skArc(sketch, "E32.trimOffspring", {"start": v(29.06, -20.5) * mm, "mid": v(29.82, -19.37) * mm, "end": v(30.54, -18.21) * mm});
            skArc(sketch, "E33.trimOffspring", {"start": v(24.16, -26.09) * mm, "mid": v(25.14, -25.14) * mm, "end": v(26.09, -24.16) * mm});
            skArc(sketch, "E34.trimOffspring", {"start": v(18.21, -30.54) * mm, "mid": v(19.37, -29.82) * mm, "end": v(20.5, -29.06) * mm});
            skArc(sketch, "E35.trimOffspring", {"start": v(11.46, -33.66) * mm, "mid": v(12.74, -33.2) * mm, "end": v(14, -32.69) * mm});
            skArc(sketch, "E36.trimOffspring", {"start": v(4.21, -35.3) * mm, "mid": v(5.56, -35.12) * mm, "end": v(6.9, -34.88) * mm});
            skArc(sketch, "E37.trimOffspring", {"start": v(-3.22, -35.41) * mm, "mid": v(-1.86, -35.51) * mm, "end": v(-0.5, -35.56) * mm});
            skArc(sketch, "E38.trimOffspring", {"start": v(-10.51, -33.97) * mm, "mid": v(-9.2, -34.35) * mm, "end": v(-7.88, -34.68) * mm});
            skArc(sketch, "E39.trimOffspring", {"start": v(-17.34, -31.04) * mm, "mid": v(-16.14, -31.68) * mm, "end": v(-14.92, -32.28) * mm});
            skArc(sketch, "E40.trimOffspring", {"start": v(-23.42, -26.76) * mm, "mid": v(-22.38, -27.64) * mm, "end": v(-21.3, -28.47) * mm});
            skArc(sketch, "E41.trimOffspring", {"start": v(-28.47, -21.3) * mm, "mid": v(-27.64, -22.38) * mm, "end": v(-26.76, -23.42) * mm});
            skArc(sketch, "E42.trimOffspring", {"start": v(-32.28, -14.92) * mm, "mid": v(-31.68, -16.14) * mm, "end": v(-31.04, -17.34) * mm});
            skArc(sketch, "E43.trimOffspring", {"start": v(-34.68, -7.88) * mm, "mid": v(-34.35, -9.2) * mm, "end": v(-33.97, -10.51) * mm});
            skSolve(sketch);
        }
        {
            var Q0;
            Q0=makeQuery(id+"F0.imprint","IMPRINT",FACE,{"disambiguationData":[TD([[makeQuery(id+"F0.imprint","IMPRINT",EDGE,{"derivedFrom":sQuery(id+"F0.wireOp",EDGE,"E0")}),1.0]])]});
            cPlane(context, id + "F1", {"entities" : qUnion([Q0]), "cplaneType" : CPlaneType.OFFSET, "offset" : 22 * mm, "width" : 152.4 * mm, "height" : 152.4 * mm});
        }
        {
            var Q0;
            Q0=qCreatedBy(id+"F1.planeOp",FACE);
            var sketch = newSketch(context, id + "F2", { "sketchPlane" : qUnion([Q0])});
            skArc(sketch, "E44", {"start": v(-2.96, 23.44) * mm, "mid": v(-3.7, 23.33) * mm, "end": v(-4.42, 23.2) * mm});
            skLineSegment(sketch, "E45", {"start": v(0, 0) * mm, "end": v(-1.82, 34.77) * mm, "construction": true});
            skLineSegment(sketch, "E46", {"start": v(-1.18, 27.04) * mm, "end": v(-1.42, 27.04) * mm});
            skLineSegment(sketch, "E47", {"start": v(0, 25.4) * mm, "end": v(0, 24.12) * mm});
            skArc(sketch, "E48.trimOffspring", {"start": v(0, 25.4) * mm, "mid": v(-0.34, 26.14) * mm, "end": v(-0.77, 26.82) * mm});
            skLineSegment(sketch, "E49.MirrorCS", {"start": v(-1.65, 27.01) * mm, "end": v(-1.42, 27.04) * mm});
            skArc(sketch, "E50.MirrorCS", {"start": v(-2.66, 25.26) * mm, "mid": v(-2.4, 26.03) * mm, "end": v(-2.04, 26.76) * mm});
            skLineSegment(sketch, "E51.MirrorCS", {"start": v(-2.66, 25.26) * mm, "end": v(-2.52, 24) * mm});
            skPoint(sketch, "E52.visualSharp", {"position": v(-1.9, 26.98) * mm});
            skArc(sketch, "E52.filletArc", {"start": v(-1.65, 27.01) * mm, "mid": v(-1.88, 26.93) * mm, "end": v(-2.04, 26.76) * mm});
            skPoint(sketch, "E53.visualSharp", {"position": v(-0.93, 27.04) * mm});
            skArc(sketch, "E53.filletArc", {"start": v(-0.77, 26.82) * mm, "mid": v(-0.95, 26.98) * mm, "end": v(-1.18, 27.04) * mm});
            skPoint(sketch, "E54.orphan", {"position": v(-2.38, 22.66) * mm});
            skPoint(sketch, "E55.orphan", {"position": v(0, 22.78) * mm});
            skPoint(sketch, "E56.visualSharp", {"position": v(-2.47, 23.5) * mm});
            skArc(sketch, "E56.filletArc", {"start": v(-2.96, 23.44) * mm, "mid": v(-2.63, 23.62) * mm, "end": v(-2.52, 24) * mm});
            skPoint(sketch, "E57.visualSharp", {"position": v(0, 23.62) * mm});
            skArc(sketch, "E57.filletArc", {"start": v(0, 24.12) * mm, "mid": v(0.15, 23.77) * mm, "end": v(0.5, 23.62) * mm});
            skArc(sketch, "E58.1.0", {"start": v(-7.77, 22.3) * mm, "mid": v(-7.48, 22.56) * mm, "end": v(-7.45, 22.94) * mm});
            skLineSegment(sketch, "E58.1.1", {"start": v(-7.85, 24.16) * mm, "end": v(-7.45, 22.94) * mm});
            skArc(sketch, "E58.1.2", {"start": v(-7.85, 24.16) * mm, "mid": v(-7.75, 24.96) * mm, "end": v(-7.56, 25.75) * mm});
            skArc(sketch, "E58.1.3", {"start": v(-7.23, 26.08) * mm, "mid": v(-7.43, 25.95) * mm, "end": v(-7.56, 25.75) * mm});
            skLineSegment(sketch, "E58.1.4", {"start": v(-7.23, 26.08) * mm, "end": v(-7, 26.15) * mm});
            skLineSegment(sketch, "E58.1.5", {"start": v(-6.78, 26.2) * mm, "end": v(-7, 26.15) * mm});
            skArc(sketch, "E58.1.6", {"start": v(-6.33, 26.08) * mm, "mid": v(-6.54, 26.2) * mm, "end": v(-6.78, 26.2) * mm});
            skArc(sketch, "E58.1.7", {"start": v(-5.28, 24.84) * mm, "mid": v(-5.77, 25.5) * mm, "end": v(-6.33, 26.08) * mm});
            skLineSegment(sketch, "E58.1.8", {"start": v(-5.28, 24.84) * mm, "end": v(-5.02, 23.6) * mm});
            skArc(sketch, "E58.1.9", {"start": v(-5.02, 23.6) * mm, "mid": v(-4.8, 23.28) * mm, "end": v(-4.42, 23.2) * mm});
            skArc(sketch, "E58.2.0", {"start": v(-12.24, 20.2) * mm, "mid": v(-12.01, 20.51) * mm, "end": v(-12.06, 20.9) * mm});
            skLineSegment(sketch, "E58.2.1", {"start": v(-12.7, 22) * mm, "end": v(-12.06, 20.9) * mm});
            skArc(sketch, "E58.2.2", {"start": v(-12.7, 22) * mm, "mid": v(-12.77, 22.8) * mm, "end": v(-12.75, 23.61) * mm});
            skArc(sketch, "E58.2.3", {"start": v(-12.5, 24) * mm, "mid": v(-12.67, 23.84) * mm, "end": v(-12.75, 23.61) * mm});
            skLineSegment(sketch, "E58.2.4", {"start": v(-12.5, 24) * mm, "end": v(-12.3, 24.12) * mm});
            skLineSegment(sketch, "E58.2.5", {"start": v(-12.07, 24.22) * mm, "end": v(-12.3, 24.12) * mm});
            skArc(sketch, "E58.2.6", {"start": v(-11.61, 24.2) * mm, "mid": v(-11.84, 24.26) * mm, "end": v(-12.07, 24.22) * mm});
            skArc(sketch, "E58.2.7", {"start": v(-10.33, 23.2) * mm, "mid": v(-10.94, 23.74) * mm, "end": v(-11.61, 24.2) * mm});
            skLineSegment(sketch, "E58.2.8", {"start": v(-10.33, 23.2) * mm, "end": v(-9.81, 22.04) * mm});
            skArc(sketch, "E58.2.9", {"start": v(-9.81, 22.04) * mm, "mid": v(-9.54, 21.77) * mm, "end": v(-9.15, 21.78) * mm});
            skArc(sketch, "E58.3.0", {"start": v(-16.17, 17.22) * mm, "mid": v(-16.01, 17.57) * mm, "end": v(-16.14, 17.93) * mm});
            skLineSegment(sketch, "E58.3.1", {"start": v(-17, 18.88) * mm, "end": v(-16.14, 17.93) * mm});
            skArc(sketch, "E58.3.2", {"start": v(-17, 18.88) * mm, "mid": v(-17.24, 19.65) * mm, "end": v(-17.38, 20.45) * mm});
            skArc(sketch, "E58.3.3", {"start": v(-17.21, 20.88) * mm, "mid": v(-17.35, 20.68) * mm, "end": v(-17.38, 20.45) * mm});
            skLineSegment(sketch, "E58.3.4", {"start": v(-17.21, 20.88) * mm, "end": v(-17.04, 21.04) * mm});
            skLineSegment(sketch, "E58.3.5", {"start": v(-16.85, 21.18) * mm, "end": v(-17.04, 21.04) * mm});
            skArc(sketch, "E58.3.6", {"start": v(-16.39, 21.25) * mm, "mid": v(-16.63, 21.27) * mm, "end": v(-16.85, 21.18) * mm});
            skArc(sketch, "E58.3.7", {"start": v(-14.93, 20.55) * mm, "mid": v(-15.64, 20.95) * mm, "end": v(-16.39, 21.25) * mm});
            skLineSegment(sketch, "E58.3.8", {"start": v(-14.93, 20.55) * mm, "end": v(-14.18, 19.52) * mm});
            skArc(sketch, "E58.3.9", {"start": v(-14.18, 19.52) * mm, "mid": v(-13.85, 19.31) * mm, "end": v(-13.48, 19.4) * mm});
            skArc(sketch, "E58.4.0", {"start": v(-19.4, 13.48) * mm, "mid": v(-19.31, 13.85) * mm, "end": v(-19.52, 14.18) * mm});
            skLineSegment(sketch, "E58.4.1", {"start": v(-20.55, 14.93) * mm, "end": v(-19.52, 14.18) * mm});
            skArc(sketch, "E58.4.2", {"start": v(-20.55, 14.93) * mm, "mid": v(-20.95, 15.64) * mm, "end": v(-21.25, 16.39) * mm});
            skArc(sketch, "E58.4.3", {"start": v(-21.18, 16.85) * mm, "mid": v(-21.27, 16.63) * mm, "end": v(-21.25, 16.39) * mm});
            skLineSegment(sketch, "E58.4.4", {"start": v(-21.18, 16.85) * mm, "end": v(-21.04, 17.04) * mm});
            skLineSegment(sketch, "E58.4.5", {"start": v(-20.88, 17.21) * mm, "end": v(-21.04, 17.04) * mm});
            skArc(sketch, "E58.4.6", {"start": v(-20.45, 17.38) * mm, "mid": v(-20.68, 17.35) * mm, "end": v(-20.88, 17.21) * mm});
            skArc(sketch, "E58.4.7", {"start": v(-18.88, 17) * mm, "mid": v(-19.65, 17.24) * mm, "end": v(-20.45, 17.38) * mm});
            skLineSegment(sketch, "E58.4.8", {"start": v(-18.88, 17) * mm, "end": v(-17.93, 16.14) * mm});
            skArc(sketch, "E58.4.9", {"start": v(-17.93, 16.14) * mm, "mid": v(-17.57, 16.01) * mm, "end": v(-17.22, 16.17) * mm});
            skArc(sketch, "E58.5.0", {"start": v(-21.78, 9.15) * mm, "mid": v(-21.77, 9.54) * mm, "end": v(-22.04, 9.81) * mm});
            skLineSegment(sketch, "E58.5.1", {"start": v(-23.2, 10.33) * mm, "end": v(-22.04, 9.81) * mm});
            skArc(sketch, "E58.5.2", {"start": v(-23.2, 10.33) * mm, "mid": v(-23.74, 10.94) * mm, "end": v(-24.2, 11.61) * mm});
            skArc(sketch, "E58.5.3", {"start": v(-24.22, 12.07) * mm, "mid": v(-24.26, 11.84) * mm, "end": v(-24.2, 11.61) * mm});
            skLineSegment(sketch, "E58.5.4", {"start": v(-24.22, 12.07) * mm, "end": v(-24.12, 12.3) * mm});
            skLineSegment(sketch, "E58.5.5", {"start": v(-24, 12.5) * mm, "end": v(-24.12, 12.3) * mm});
            skArc(sketch, "E58.5.6", {"start": v(-23.61, 12.75) * mm, "mid": v(-23.84, 12.67) * mm, "end": v(-24, 12.5) * mm});
            skArc(sketch, "E58.5.7", {"start": v(-22, 12.7) * mm, "mid": v(-22.8, 12.77) * mm, "end": v(-23.61, 12.75) * mm});
            skLineSegment(sketch, "E58.5.8", {"start": v(-22, 12.7) * mm, "end": v(-20.9, 12.06) * mm});
            skArc(sketch, "E58.5.9", {"start": v(-20.9, 12.06) * mm, "mid": v(-20.51, 12.01) * mm, "end": v(-20.2, 12.24) * mm});
            skArc(sketch, "E58.6.0", {"start": v(-23.2, 4.42) * mm, "mid": v(-23.28, 4.8) * mm, "end": v(-23.6, 5.02) * mm});
            skLineSegment(sketch, "E58.6.1", {"start": v(-24.84, 5.28) * mm, "end": v(-23.6, 5.02) * mm});
            skArc(sketch, "E58.6.2", {"start": v(-24.84, 5.28) * mm, "mid": v(-25.5, 5.77) * mm, "end": v(-26.08, 6.33) * mm});
            skArc(sketch, "E58.6.3", {"start": v(-26.2, 6.78) * mm, "mid": v(-26.2, 6.54) * mm, "end": v(-26.08, 6.33) * mm});
            skLineSegment(sketch, "E58.6.4", {"start": v(-26.2, 6.78) * mm, "end": v(-26.15, 7) * mm});
            skLineSegment(sketch, "E58.6.5", {"start": v(-26.08, 7.23) * mm, "end": v(-26.15, 7) * mm});
            skArc(sketch, "E58.6.6", {"start": v(-25.75, 7.56) * mm, "mid": v(-25.95, 7.43) * mm, "end": v(-26.08, 7.23) * mm});
            skArc(sketch, "E58.6.7", {"start": v(-24.16, 7.85) * mm, "mid": v(-24.96, 7.75) * mm, "end": v(-25.75, 7.56) * mm});
            skLineSegment(sketch, "E58.6.8", {"start": v(-24.16, 7.85) * mm, "end": v(-22.94, 7.45) * mm});
            skArc(sketch, "E58.6.9", {"start": v(-22.94, 7.45) * mm, "mid": v(-22.56, 7.48) * mm, "end": v(-22.3, 7.77) * mm});
            skArc(sketch, "E58.7.0", {"start": v(-23.62, -0.5) * mm, "mid": v(-23.77, -0.15) * mm, "end": v(-24.12, 0) * mm});
            skLineSegment(sketch, "E58.7.1", {"start": v(-25.4, 0) * mm, "end": v(-24.12, 0) * mm});
            skArc(sketch, "E58.7.2", {"start": v(-25.4, 0) * mm, "mid": v(-26.14, 0.34) * mm, "end": v(-26.82, 0.77) * mm});
            skArc(sketch, "E58.7.3", {"start": v(-27.04, 1.18) * mm, "mid": v(-26.98, 0.95) * mm, "end": v(-26.82, 0.77) * mm});
            skLineSegment(sketch, "E58.7.4", {"start": v(-27.04, 1.18) * mm, "end": v(-27.04, 1.42) * mm});
            skLineSegment(sketch, "E58.7.5", {"start": v(-27.01, 1.65) * mm, "end": v(-27.04, 1.42) * mm});
            skArc(sketch, "E58.7.6", {"start": v(-26.76, 2.04) * mm, "mid": v(-26.93, 1.88) * mm, "end": v(-27.01, 1.65) * mm});
            skArc(sketch, "E58.7.7", {"start": v(-25.26, 2.66) * mm, "mid": v(-26.03, 2.4) * mm, "end": v(-26.76, 2.04) * mm});
            skLineSegment(sketch, "E58.7.8", {"start": v(-25.26, 2.66) * mm, "end": v(-24, 2.52) * mm});
            skArc(sketch, "E58.7.9", {"start": v(-24, 2.52) * mm, "mid": v(-23.62, 2.63) * mm, "end": v(-23.44, 2.96) * mm});
            skArc(sketch, "E58.8.0", {"start": v(-23, -5.4) * mm, "mid": v(-23.22, -5.08) * mm, "end": v(-23.6, -5.02) * mm});
            skLineSegment(sketch, "E58.8.1", {"start": v(-24.84, -5.28) * mm, "end": v(-23.6, -5.02) * mm});
            skArc(sketch, "E58.8.2", {"start": v(-24.84, -5.28) * mm, "mid": v(-25.64, -5.1) * mm, "end": v(-26.4, -4.83) * mm});
            skArc(sketch, "E58.8.3", {"start": v(-26.69, -4.47) * mm, "mid": v(-26.59, -4.68) * mm, "end": v(-26.4, -4.83) * mm});
            skLineSegment(sketch, "E58.8.4", {"start": v(-26.69, -4.47) * mm, "end": v(-26.74, -4.24) * mm});
            skLineSegment(sketch, "E58.8.5", {"start": v(-26.76, -4) * mm, "end": v(-26.74, -4.24) * mm});
            skArc(sketch, "E58.8.6", {"start": v(-26.6, -3.57) * mm, "mid": v(-26.73, -3.76) * mm, "end": v(-26.76, -4) * mm});
            skArc(sketch, "E58.8.7", {"start": v(-25.26, -2.66) * mm, "mid": v(-25.96, -3.07) * mm, "end": v(-26.6, -3.57) * mm});
            skLineSegment(sketch, "E58.8.8", {"start": v(-25.26, -2.66) * mm, "end": v(-24, -2.52) * mm});
            skArc(sketch, "E58.8.9", {"start": v(-24, -2.52) * mm, "mid": v(-23.65, -2.34) * mm, "end": v(-23.54, -1.97) * mm});
            skArc(sketch, "E58.9.0", {"start": v(-21.37, -10.06) * mm, "mid": v(-21.66, -9.8) * mm, "end": v(-22.04, -9.81) * mm});
            skLineSegment(sketch, "E58.9.1", {"start": v(-23.2, -10.33) * mm, "end": v(-22.04, -9.81) * mm});
            skArc(sketch, "E58.9.2", {"start": v(-23.2, -10.33) * mm, "mid": v(-24.01, -10.32) * mm, "end": v(-24.82, -10.2) * mm});
            skArc(sketch, "E58.9.3", {"start": v(-25.18, -9.92) * mm, "mid": v(-25.03, -10.1) * mm, "end": v(-24.82, -10.2) * mm});
            skLineSegment(sketch, "E58.9.4", {"start": v(-25.18, -9.92) * mm, "end": v(-25.27, -9.7) * mm});
            skLineSegment(sketch, "E58.9.5", {"start": v(-25.35, -9.48) * mm, "end": v(-25.27, -9.7) * mm});
            skArc(sketch, "E58.9.6", {"start": v(-25.27, -9.02) * mm, "mid": v(-25.37, -9.24) * mm, "end": v(-25.35, -9.48) * mm});
            skArc(sketch, "E58.9.7", {"start": v(-24.16, -7.85) * mm, "mid": v(-24.75, -8.4) * mm, "end": v(-25.27, -9.02) * mm});
            skLineSegment(sketch, "E58.9.8", {"start": v(-24.16, -7.85) * mm, "end": v(-22.94, -7.45) * mm});
            skArc(sketch, "E58.9.9", {"start": v(-22.94, -7.45) * mm, "mid": v(-22.65, -7.2) * mm, "end": v(-22.61, -6.83) * mm});
            skArc(sketch, "E58.10.0", {"start": v(-18.81, -14.28) * mm, "mid": v(-19.14, -14.09) * mm, "end": v(-19.52, -14.18) * mm});
            skLineSegment(sketch, "E58.10.1", {"start": v(-20.55, -14.93) * mm, "end": v(-19.52, -14.18) * mm});
            skArc(sketch, "E58.10.2", {"start": v(-20.55, -14.93) * mm, "mid": v(-21.34, -15.09) * mm, "end": v(-22.15, -15.14) * mm});
            skArc(sketch, "E58.10.3", {"start": v(-22.57, -14.94) * mm, "mid": v(-22.38, -15.1) * mm, "end": v(-22.15, -15.14) * mm});
            skLineSegment(sketch, "E58.10.4", {"start": v(-22.57, -14.94) * mm, "end": v(-22.7, -14.74) * mm});
            skLineSegment(sketch, "E58.10.5", {"start": v(-22.82, -14.54) * mm, "end": v(-22.7, -14.74) * mm});
            skArc(sketch, "E58.10.6", {"start": v(-22.85, -14.08) * mm, "mid": v(-22.9, -14.31) * mm, "end": v(-22.82, -14.54) * mm});
            skArc(sketch, "E58.10.7", {"start": v(-22, -12.7) * mm, "mid": v(-22.47, -13.36) * mm, "end": v(-22.85, -14.08) * mm});
            skLineSegment(sketch, "E58.10.8", {"start": v(-22, -12.7) * mm, "end": v(-20.9, -12.06) * mm});
            skArc(sketch, "E58.10.9", {"start": v(-20.9, -12.06) * mm, "mid": v(-20.66, -11.76) * mm, "end": v(-20.7, -11.38) * mm});
            skArc(sketch, "E58.11.0", {"start": v(-15.43, -17.88) * mm, "mid": v(-15.8, -17.76) * mm, "end": v(-16.14, -17.93) * mm});
            skLineSegment(sketch, "E58.11.1", {"start": v(-17, -18.88) * mm, "end": v(-16.14, -17.93) * mm});
            skArc(sketch, "E58.11.2", {"start": v(-17, -18.88) * mm, "mid": v(-17.74, -19.2) * mm, "end": v(-18.52, -19.42) * mm});
            skArc(sketch, "E58.11.3", {"start": v(-18.97, -19.3) * mm, "mid": v(-18.76, -19.41) * mm, "end": v(-18.52, -19.42) * mm});
            skLineSegment(sketch, "E58.11.4", {"start": v(-18.97, -19.3) * mm, "end": v(-19.14, -19.14) * mm});
            skLineSegment(sketch, "E58.11.5", {"start": v(-19.3, -18.97) * mm, "end": v(-19.14, -19.14) * mm});
            skArc(sketch, "E58.11.6", {"start": v(-19.42, -18.52) * mm, "mid": v(-19.41, -18.76) * mm, "end": v(-19.3, -18.97) * mm});
            skArc(sketch, "E58.11.7", {"start": v(-18.88, -17) * mm, "mid": v(-19.2, -17.74) * mm, "end": v(-19.42, -18.52) * mm});
            skLineSegment(sketch, "E58.11.8", {"start": v(-18.88, -17) * mm, "end": v(-17.93, -16.14) * mm});
            skArc(sketch, "E58.11.9", {"start": v(-17.93, -16.14) * mm, "mid": v(-17.76, -15.8) * mm, "end": v(-17.88, -15.43) * mm});
            skArc(sketch, "E58.12.0", {"start": v(-11.38, -20.7) * mm, "mid": v(-11.76, -20.66) * mm, "end": v(-12.06, -20.9) * mm});
            skLineSegment(sketch, "E58.12.1", {"start": v(-12.7, -22) * mm, "end": v(-12.06, -20.9) * mm});
            skArc(sketch, "E58.12.2", {"start": v(-12.7, -22) * mm, "mid": v(-13.36, -22.47) * mm, "end": v(-14.08, -22.85) * mm});
            skArc(sketch, "E58.12.3", {"start": v(-14.54, -22.82) * mm, "mid": v(-14.31, -22.9) * mm, "end": v(-14.08, -22.85) * mm});
            skLineSegment(sketch, "E58.12.4", {"start": v(-14.54, -22.82) * mm, "end": v(-14.74, -22.7) * mm});
            skLineSegment(sketch, "E58.12.5", {"start": v(-14.94, -22.57) * mm, "end": v(-14.74, -22.7) * mm});
            skArc(sketch, "E58.12.6", {"start": v(-15.14, -22.15) * mm, "mid": v(-15.1, -22.38) * mm, "end": v(-14.94, -22.57) * mm});
            skArc(sketch, "E58.12.7", {"start": v(-14.93, -20.55) * mm, "mid": v(-15.09, -21.34) * mm, "end": v(-15.14, -22.15) * mm});
            skLineSegment(sketch, "E58.12.8", {"start": v(-14.93, -20.55) * mm, "end": v(-14.18, -19.52) * mm});
            skArc(sketch, "E58.12.9", {"start": v(-14.18, -19.52) * mm, "mid": v(-14.09, -19.14) * mm, "end": v(-14.28, -18.81) * mm});
            skArc(sketch, "E58.13.0", {"start": v(-6.83, -22.61) * mm, "mid": v(-7.2, -22.65) * mm, "end": v(-7.45, -22.94) * mm});
            skLineSegment(sketch, "E58.13.1", {"start": v(-7.85, -24.16) * mm, "end": v(-7.45, -22.94) * mm});
            skArc(sketch, "E58.13.2", {"start": v(-7.85, -24.16) * mm, "mid": v(-8.4, -24.75) * mm, "end": v(-9.02, -25.27) * mm});
            skArc(sketch, "E58.13.3", {"start": v(-9.48, -25.35) * mm, "mid": v(-9.24, -25.37) * mm, "end": v(-9.02, -25.27) * mm});
            skLineSegment(sketch, "E58.13.4", {"start": v(-9.48, -25.35) * mm, "end": v(-9.7, -25.27) * mm});
            skLineSegment(sketch, "E58.13.5", {"start": v(-9.92, -25.18) * mm, "end": v(-9.7, -25.27) * mm});
            skArc(sketch, "E58.13.6", {"start": v(-10.2, -24.82) * mm, "mid": v(-10.1, -25.03) * mm, "end": v(-9.92, -25.18) * mm});
            skArc(sketch, "E58.13.7", {"start": v(-10.33, -23.2) * mm, "mid": v(-10.32, -24.01) * mm, "end": v(-10.2, -24.82) * mm});
            skLineSegment(sketch, "E58.13.8", {"start": v(-10.33, -23.2) * mm, "end": v(-9.81, -22.04) * mm});
            skArc(sketch, "E58.13.9", {"start": v(-9.81, -22.04) * mm, "mid": v(-9.8, -21.66) * mm, "end": v(-10.06, -21.37) * mm});
            skArc(sketch, "E58.14.0", {"start": v(-1.97, -23.54) * mm, "mid": v(-2.34, -23.65) * mm, "end": v(-2.52, -24) * mm});
            skLineSegment(sketch, "E58.14.1", {"start": v(-2.66, -25.26) * mm, "end": v(-2.52, -24) * mm});
            skArc(sketch, "E58.14.2", {"start": v(-2.66, -25.26) * mm, "mid": v(-3.07, -25.96) * mm, "end": v(-3.57, -26.6) * mm});
            skArc(sketch, "E58.14.3", {"start": v(-4, -26.76) * mm, "mid": v(-3.76, -26.73) * mm, "end": v(-3.57, -26.6) * mm});
            skLineSegment(sketch, "E58.14.4", {"start": v(-4, -26.76) * mm, "end": v(-4.24, -26.74) * mm});
            skLineSegment(sketch, "E58.14.5", {"start": v(-4.47, -26.69) * mm, "end": v(-4.24, -26.74) * mm});
            skArc(sketch, "E58.14.6", {"start": v(-4.83, -26.4) * mm, "mid": v(-4.68, -26.59) * mm, "end": v(-4.47, -26.69) * mm});
            skArc(sketch, "E58.14.7", {"start": v(-5.28, -24.84) * mm, "mid": v(-5.1, -25.64) * mm, "end": v(-4.83, -26.4) * mm});
            skLineSegment(sketch, "E58.14.8", {"start": v(-5.28, -24.84) * mm, "end": v(-5.02, -23.6) * mm});
            skArc(sketch, "E58.14.9", {"start": v(-5.02, -23.6) * mm, "mid": v(-5.08, -23.22) * mm, "end": v(-5.4, -23) * mm});
            skArc(sketch, "E58.15.0", {"start": v(2.96, -23.44) * mm, "mid": v(2.63, -23.62) * mm, "end": v(2.52, -24) * mm});
            skLineSegment(sketch, "E58.15.1", {"start": v(2.66, -25.26) * mm, "end": v(2.52, -24) * mm});
            skArc(sketch, "E58.15.2", {"start": v(2.66, -25.26) * mm, "mid": v(2.4, -26.03) * mm, "end": v(2.04, -26.76) * mm});
            skArc(sketch, "E58.15.3", {"start": v(1.65, -27.01) * mm, "mid": v(1.88, -26.93) * mm, "end": v(2.04, -26.76) * mm});
            skLineSegment(sketch, "E58.15.4", {"start": v(1.65, -27.01) * mm, "end": v(1.42, -27.04) * mm});
            skLineSegment(sketch, "E58.15.5", {"start": v(1.18, -27.04) * mm, "end": v(1.42, -27.04) * mm});
            skArc(sketch, "E58.15.6", {"start": v(0.77, -26.82) * mm, "mid": v(0.95, -26.98) * mm, "end": v(1.18, -27.04) * mm});
            skArc(sketch, "E58.15.7", {"start": v(0, -25.4) * mm, "mid": v(0.34, -26.14) * mm, "end": v(0.77, -26.82) * mm});
            skLineSegment(sketch, "E58.15.8", {"start": v(0, -25.4) * mm, "end": v(0, -24.12) * mm});
            skArc(sketch, "E58.15.9", {"start": v(0, -24.12) * mm, "mid": v(-0.15, -23.77) * mm, "end": v(-0.5, -23.62) * mm});
            skArc(sketch, "E58.16.0", {"start": v(7.77, -22.3) * mm, "mid": v(7.48, -22.56) * mm, "end": v(7.45, -22.94) * mm});
            skLineSegment(sketch, "E58.16.1", {"start": v(7.85, -24.16) * mm, "end": v(7.45, -22.94) * mm});
            skArc(sketch, "E58.16.2", {"start": v(7.85, -24.16) * mm, "mid": v(7.75, -24.96) * mm, "end": v(7.56, -25.75) * mm});
            skArc(sketch, "E58.16.3", {"start": v(7.23, -26.08) * mm, "mid": v(7.43, -25.95) * mm, "end": v(7.56, -25.75) * mm});
            skLineSegment(sketch, "E58.16.4", {"start": v(7.23, -26.08) * mm, "end": v(7, -26.15) * mm});
            skLineSegment(sketch, "E58.16.5", {"start": v(6.78, -26.2) * mm, "end": v(7, -26.15) * mm});
            skArc(sketch, "E58.16.6", {"start": v(6.33, -26.08) * mm, "mid": v(6.54, -26.2) * mm, "end": v(6.78, -26.2) * mm});
            skArc(sketch, "E58.16.7", {"start": v(5.28, -24.84) * mm, "mid": v(5.77, -25.5) * mm, "end": v(6.33, -26.08) * mm});
            skLineSegment(sketch, "E58.16.8", {"start": v(5.28, -24.84) * mm, "end": v(5.02, -23.6) * mm});
            skArc(sketch, "E58.16.9", {"start": v(5.02, -23.6) * mm, "mid": v(4.8, -23.28) * mm, "end": v(4.42, -23.2) * mm});
            skArc(sketch, "E58.17.0", {"start": v(12.24, -20.2) * mm, "mid": v(12.01, -20.51) * mm, "end": v(12.06, -20.9) * mm});
            skLineSegment(sketch, "E58.17.1", {"start": v(12.7, -22) * mm, "end": v(12.06, -20.9) * mm});
            skArc(sketch, "E58.17.2", {"start": v(12.7, -22) * mm, "mid": v(12.77, -22.8) * mm, "end": v(12.75, -23.61) * mm});
            skArc(sketch, "E58.17.3", {"start": v(12.5, -24) * mm, "mid": v(12.67, -23.84) * mm, "end": v(12.75, -23.61) * mm});
            skLineSegment(sketch, "E58.17.4", {"start": v(12.5, -24) * mm, "end": v(12.3, -24.12) * mm});
            skLineSegment(sketch, "E58.17.5", {"start": v(12.07, -24.22) * mm, "end": v(12.3, -24.12) * mm});
            skArc(sketch, "E58.17.6", {"start": v(11.61, -24.2) * mm, "mid": v(11.84, -24.26) * mm, "end": v(12.07, -24.22) * mm});
            skArc(sketch, "E58.17.7", {"start": v(10.33, -23.2) * mm, "mid": v(10.94, -23.74) * mm, "end": v(11.61, -24.2) * mm});
            skLineSegment(sketch, "E58.17.8", {"start": v(10.33, -23.2) * mm, "end": v(9.81, -22.04) * mm});
            skArc(sketch, "E58.17.9", {"start": v(9.81, -22.04) * mm, "mid": v(9.54, -21.77) * mm, "end": v(9.15, -21.78) * mm});
            skArc(sketch, "E58.18.0", {"start": v(16.17, -17.22) * mm, "mid": v(16.01, -17.57) * mm, "end": v(16.14, -17.93) * mm});
            skLineSegment(sketch, "E58.18.1", {"start": v(17, -18.88) * mm, "end": v(16.14, -17.93) * mm});
            skArc(sketch, "E58.18.2", {"start": v(17, -18.88) * mm, "mid": v(17.24, -19.65) * mm, "end": v(17.38, -20.45) * mm});
            skArc(sketch, "E58.18.3", {"start": v(17.21, -20.88) * mm, "mid": v(17.35, -20.68) * mm, "end": v(17.38, -20.45) * mm});
            skLineSegment(sketch, "E58.18.4", {"start": v(17.21, -20.88) * mm, "end": v(17.04, -21.04) * mm});
            skLineSegment(sketch, "E58.18.5", {"start": v(16.85, -21.18) * mm, "end": v(17.04, -21.04) * mm});
            skArc(sketch, "E58.18.6", {"start": v(16.39, -21.25) * mm, "mid": v(16.63, -21.27) * mm, "end": v(16.85, -21.18) * mm});
            skArc(sketch, "E58.18.7", {"start": v(14.93, -20.55) * mm, "mid": v(15.64, -20.95) * mm, "end": v(16.39, -21.25) * mm});
            skLineSegment(sketch, "E58.18.8", {"start": v(14.93, -20.55) * mm, "end": v(14.18, -19.52) * mm});
            skArc(sketch, "E58.18.9", {"start": v(14.18, -19.52) * mm, "mid": v(13.85, -19.31) * mm, "end": v(13.48, -19.4) * mm});
            skArc(sketch, "E58.19.0", {"start": v(19.4, -13.48) * mm, "mid": v(19.31, -13.85) * mm, "end": v(19.52, -14.18) * mm});
            skLineSegment(sketch, "E58.19.1", {"start": v(20.55, -14.93) * mm, "end": v(19.52, -14.18) * mm});
            skArc(sketch, "E58.19.2", {"start": v(20.55, -14.93) * mm, "mid": v(20.95, -15.64) * mm, "end": v(21.25, -16.39) * mm});
            skArc(sketch, "E58.19.3", {"start": v(21.18, -16.85) * mm, "mid": v(21.27, -16.63) * mm, "end": v(21.25, -16.39) * mm});
            skLineSegment(sketch, "E58.19.4", {"start": v(21.18, -16.85) * mm, "end": v(21.04, -17.04) * mm});
            skLineSegment(sketch, "E58.19.5", {"start": v(20.88, -17.21) * mm, "end": v(21.04, -17.04) * mm});
            skArc(sketch, "E58.19.6", {"start": v(20.45, -17.38) * mm, "mid": v(20.68, -17.35) * mm, "end": v(20.88, -17.21) * mm});
            skArc(sketch, "E58.19.7", {"start": v(18.88, -17) * mm, "mid": v(19.65, -17.24) * mm, "end": v(20.45, -17.38) * mm});
            skLineSegment(sketch, "E58.19.8", {"start": v(18.88, -17) * mm, "end": v(17.93, -16.14) * mm});
            skArc(sketch, "E58.19.9", {"start": v(17.93, -16.14) * mm, "mid": v(17.57, -16.01) * mm, "end": v(17.22, -16.17) * mm});
            skArc(sketch, "E58.20.0", {"start": v(21.78, -9.15) * mm, "mid": v(21.77, -9.54) * mm, "end": v(22.04, -9.81) * mm});
            skLineSegment(sketch, "E58.20.1", {"start": v(23.2, -10.33) * mm, "end": v(22.04, -9.81) * mm});
            skArc(sketch, "E58.20.2", {"start": v(23.2, -10.33) * mm, "mid": v(23.74, -10.94) * mm, "end": v(24.2, -11.61) * mm});
            skArc(sketch, "E58.20.3", {"start": v(24.22, -12.07) * mm, "mid": v(24.26, -11.84) * mm, "end": v(24.2, -11.61) * mm});
            skLineSegment(sketch, "E58.20.4", {"start": v(24.22, -12.07) * mm, "end": v(24.12, -12.3) * mm});
            skLineSegment(sketch, "E58.20.5", {"start": v(24, -12.5) * mm, "end": v(24.12, -12.3) * mm});
            skArc(sketch, "E58.20.6", {"start": v(23.61, -12.75) * mm, "mid": v(23.84, -12.67) * mm, "end": v(24, -12.5) * mm});
            skArc(sketch, "E58.20.7", {"start": v(22, -12.7) * mm, "mid": v(22.8, -12.77) * mm, "end": v(23.61, -12.75) * mm});
            skLineSegment(sketch, "E58.20.8", {"start": v(22, -12.7) * mm, "end": v(20.9, -12.06) * mm});
            skArc(sketch, "E58.20.9", {"start": v(20.9, -12.06) * mm, "mid": v(20.51, -12.01) * mm, "end": v(20.2, -12.24) * mm});
            skArc(sketch, "E58.21.0", {"start": v(23.2, -4.42) * mm, "mid": v(23.28, -4.8) * mm, "end": v(23.6, -5.02) * mm});
            skLineSegment(sketch, "E58.21.1", {"start": v(24.84, -5.28) * mm, "end": v(23.6, -5.02) * mm});
            skArc(sketch, "E58.21.2", {"start": v(24.84, -5.28) * mm, "mid": v(25.5, -5.77) * mm, "end": v(26.08, -6.33) * mm});
            skArc(sketch, "E58.21.3", {"start": v(26.2, -6.78) * mm, "mid": v(26.2, -6.54) * mm, "end": v(26.08, -6.33) * mm});
            skLineSegment(sketch, "E58.21.4", {"start": v(26.2, -6.78) * mm, "end": v(26.15, -7) * mm});
            skLineSegment(sketch, "E58.21.5", {"start": v(26.08, -7.23) * mm, "end": v(26.15, -7) * mm});
            skArc(sketch, "E58.21.6", {"start": v(25.75, -7.56) * mm, "mid": v(25.95, -7.43) * mm, "end": v(26.08, -7.23) * mm});
            skArc(sketch, "E58.21.7", {"start": v(24.16, -7.85) * mm, "mid": v(24.96, -7.75) * mm, "end": v(25.75, -7.56) * mm});
            skLineSegment(sketch, "E58.21.8", {"start": v(24.16, -7.85) * mm, "end": v(22.94, -7.45) * mm});
            skArc(sketch, "E58.21.9", {"start": v(22.94, -7.45) * mm, "mid": v(22.56, -7.48) * mm, "end": v(22.3, -7.77) * mm});
            skArc(sketch, "E58.22.0", {"start": v(23.62, 0.5) * mm, "mid": v(23.77, 0.15) * mm, "end": v(24.12, 0) * mm});
            skLineSegment(sketch, "E58.22.1", {"start": v(25.4, 0) * mm, "end": v(24.12, 0) * mm});
            skArc(sketch, "E58.22.2", {"start": v(25.4, 0) * mm, "mid": v(26.14, -0.34) * mm, "end": v(26.82, -0.77) * mm});
            skArc(sketch, "E58.22.3", {"start": v(27.04, -1.18) * mm, "mid": v(26.98, -0.95) * mm, "end": v(26.82, -0.77) * mm});
            skLineSegment(sketch, "E58.22.4", {"start": v(27.04, -1.18) * mm, "end": v(27.04, -1.42) * mm});
            skLineSegment(sketch, "E58.22.5", {"start": v(27.01, -1.65) * mm, "end": v(27.04, -1.42) * mm});
            skArc(sketch, "E58.22.6", {"start": v(26.76, -2.04) * mm, "mid": v(26.93, -1.88) * mm, "end": v(27.01, -1.65) * mm});
            skArc(sketch, "E58.22.7", {"start": v(25.26, -2.66) * mm, "mid": v(26.03, -2.4) * mm, "end": v(26.76, -2.04) * mm});
            skLineSegment(sketch, "E58.22.8", {"start": v(25.26, -2.66) * mm, "end": v(24, -2.52) * mm});
            skArc(sketch, "E58.22.9", {"start": v(24, -2.52) * mm, "mid": v(23.62, -2.63) * mm, "end": v(23.44, -2.96) * mm});
            skArc(sketch, "E58.23.0", {"start": v(23, 5.4) * mm, "mid": v(23.22, 5.08) * mm, "end": v(23.6, 5.02) * mm});
            skLineSegment(sketch, "E58.23.1", {"start": v(24.84, 5.28) * mm, "end": v(23.6, 5.02) * mm});
            skArc(sketch, "E58.23.2", {"start": v(24.84, 5.28) * mm, "mid": v(25.64, 5.1) * mm, "end": v(26.4, 4.83) * mm});
            skArc(sketch, "E58.23.3", {"start": v(26.69, 4.47) * mm, "mid": v(26.59, 4.68) * mm, "end": v(26.4, 4.83) * mm});
            skLineSegment(sketch, "E58.23.4", {"start": v(26.69, 4.47) * mm, "end": v(26.74, 4.24) * mm});
            skLineSegment(sketch, "E58.23.5", {"start": v(26.76, 4) * mm, "end": v(26.74, 4.24) * mm});
            skArc(sketch, "E58.23.6", {"start": v(26.6, 3.57) * mm, "mid": v(26.73, 3.76) * mm, "end": v(26.76, 4) * mm});
            skArc(sketch, "E58.23.7", {"start": v(25.26, 2.66) * mm, "mid": v(25.96, 3.07) * mm, "end": v(26.6, 3.57) * mm});
            skLineSegment(sketch, "E58.23.8", {"start": v(25.26, 2.66) * mm, "end": v(24, 2.52) * mm});
            skArc(sketch, "E58.23.9", {"start": v(24, 2.52) * mm, "mid": v(23.65, 2.34) * mm, "end": v(23.54, 1.97) * mm});
            skArc(sketch, "E58.24.0", {"start": v(21.37, 10.06) * mm, "mid": v(21.66, 9.8) * mm, "end": v(22.04, 9.81) * mm});
            skLineSegment(sketch, "E58.24.1", {"start": v(23.2, 10.33) * mm, "end": v(22.04, 9.81) * mm});
            skArc(sketch, "E58.24.2", {"start": v(23.2, 10.33) * mm, "mid": v(24.01, 10.32) * mm, "end": v(24.82, 10.2) * mm});
            skArc(sketch, "E58.24.3", {"start": v(25.18, 9.92) * mm, "mid": v(25.03, 10.1) * mm, "end": v(24.82, 10.2) * mm});
            skLineSegment(sketch, "E58.24.4", {"start": v(25.18, 9.92) * mm, "end": v(25.27, 9.7) * mm});
            skLineSegment(sketch, "E58.24.5", {"start": v(25.35, 9.48) * mm, "end": v(25.27, 9.7) * mm});
            skArc(sketch, "E58.24.6", {"start": v(25.27, 9.02) * mm, "mid": v(25.37, 9.24) * mm, "end": v(25.35, 9.48) * mm});
            skArc(sketch, "E58.24.7", {"start": v(24.16, 7.85) * mm, "mid": v(24.75, 8.4) * mm, "end": v(25.27, 9.02) * mm});
            skLineSegment(sketch, "E58.24.8", {"start": v(24.16, 7.85) * mm, "end": v(22.94, 7.45) * mm});
            skArc(sketch, "E58.24.9", {"start": v(22.94, 7.45) * mm, "mid": v(22.65, 7.2) * mm, "end": v(22.61, 6.83) * mm});
            skArc(sketch, "E58.25.0", {"start": v(18.81, 14.28) * mm, "mid": v(19.14, 14.09) * mm, "end": v(19.52, 14.18) * mm});
            skLineSegment(sketch, "E58.25.1", {"start": v(20.55, 14.93) * mm, "end": v(19.52, 14.18) * mm});
            skArc(sketch, "E58.25.2", {"start": v(20.55, 14.93) * mm, "mid": v(21.34, 15.09) * mm, "end": v(22.15, 15.14) * mm});
            skArc(sketch, "E58.25.3", {"start": v(22.57, 14.94) * mm, "mid": v(22.38, 15.1) * mm, "end": v(22.15, 15.14) * mm});
            skLineSegment(sketch, "E58.25.4", {"start": v(22.57, 14.94) * mm, "end": v(22.7, 14.74) * mm});
            skLineSegment(sketch, "E58.25.5", {"start": v(22.82, 14.54) * mm, "end": v(22.7, 14.74) * mm});
            skArc(sketch, "E58.25.6", {"start": v(22.85, 14.08) * mm, "mid": v(22.9, 14.31) * mm, "end": v(22.82, 14.54) * mm});
            skArc(sketch, "E58.25.7", {"start": v(22, 12.7) * mm, "mid": v(22.47, 13.36) * mm, "end": v(22.85, 14.08) * mm});
            skLineSegment(sketch, "E58.25.8", {"start": v(22, 12.7) * mm, "end": v(20.9, 12.06) * mm});
            skArc(sketch, "E58.25.9", {"start": v(20.9, 12.06) * mm, "mid": v(20.66, 11.76) * mm, "end": v(20.7, 11.38) * mm});
            skArc(sketch, "E58.26.0", {"start": v(15.43, 17.88) * mm, "mid": v(15.8, 17.76) * mm, "end": v(16.14, 17.93) * mm});
            skLineSegment(sketch, "E58.26.1", {"start": v(17, 18.88) * mm, "end": v(16.14, 17.93) * mm});
            skArc(sketch, "E58.26.2", {"start": v(17, 18.88) * mm, "mid": v(17.74, 19.2) * mm, "end": v(18.52, 19.42) * mm});
            skArc(sketch, "E58.26.3", {"start": v(18.97, 19.3) * mm, "mid": v(18.76, 19.41) * mm, "end": v(18.52, 19.42) * mm});
            skLineSegment(sketch, "E58.26.4", {"start": v(18.97, 19.3) * mm, "end": v(19.14, 19.14) * mm});
            skLineSegment(sketch, "E58.26.5", {"start": v(19.3, 18.97) * mm, "end": v(19.14, 19.14) * mm});
            skArc(sketch, "E58.26.6", {"start": v(19.42, 18.52) * mm, "mid": v(19.41, 18.76) * mm, "end": v(19.3, 18.97) * mm});
            skArc(sketch, "E58.26.7", {"start": v(18.88, 17) * mm, "mid": v(19.2, 17.74) * mm, "end": v(19.42, 18.52) * mm});
            skLineSegment(sketch, "E58.26.8", {"start": v(18.88, 17) * mm, "end": v(17.93, 16.14) * mm});
            skArc(sketch, "E58.26.9", {"start": v(17.93, 16.14) * mm, "mid": v(17.76, 15.8) * mm, "end": v(17.88, 15.43) * mm});
            skArc(sketch, "E58.27.0", {"start": v(11.38, 20.7) * mm, "mid": v(11.76, 20.66) * mm, "end": v(12.06, 20.9) * mm});
            skLineSegment(sketch, "E58.27.1", {"start": v(12.7, 22) * mm, "end": v(12.06, 20.9) * mm});
            skArc(sketch, "E58.27.2", {"start": v(12.7, 22) * mm, "mid": v(13.36, 22.47) * mm, "end": v(14.08, 22.85) * mm});
            skArc(sketch, "E58.27.3", {"start": v(14.54, 22.82) * mm, "mid": v(14.31, 22.9) * mm, "end": v(14.08, 22.85) * mm});
            skLineSegment(sketch, "E58.27.4", {"start": v(14.54, 22.82) * mm, "end": v(14.74, 22.7) * mm});
            skLineSegment(sketch, "E58.27.5", {"start": v(14.94, 22.57) * mm, "end": v(14.74, 22.7) * mm});
            skArc(sketch, "E58.27.6", {"start": v(15.14, 22.15) * mm, "mid": v(15.1, 22.38) * mm, "end": v(14.94, 22.57) * mm});
            skArc(sketch, "E58.27.7", {"start": v(14.93, 20.55) * mm, "mid": v(15.09, 21.34) * mm, "end": v(15.14, 22.15) * mm});
            skLineSegment(sketch, "E58.27.8", {"start": v(14.93, 20.55) * mm, "end": v(14.18, 19.52) * mm});
            skArc(sketch, "E58.27.9", {"start": v(14.18, 19.52) * mm, "mid": v(14.09, 19.14) * mm, "end": v(14.28, 18.81) * mm});
            skArc(sketch, "E58.28.0", {"start": v(6.83, 22.61) * mm, "mid": v(7.2, 22.65) * mm, "end": v(7.45, 22.94) * mm});
            skLineSegment(sketch, "E58.28.1", {"start": v(7.85, 24.16) * mm, "end": v(7.45, 22.94) * mm});
            skArc(sketch, "E58.28.2", {"start": v(7.85, 24.16) * mm, "mid": v(8.4, 24.75) * mm, "end": v(9.02, 25.27) * mm});
            skArc(sketch, "E58.28.3", {"start": v(9.48, 25.35) * mm, "mid": v(9.24, 25.37) * mm, "end": v(9.02, 25.27) * mm});
            skLineSegment(sketch, "E58.28.4", {"start": v(9.48, 25.35) * mm, "end": v(9.7, 25.27) * mm});
            skLineSegment(sketch, "E58.28.5", {"start": v(9.92, 25.18) * mm, "end": v(9.7, 25.27) * mm});
            skArc(sketch, "E58.28.6", {"start": v(10.2, 24.82) * mm, "mid": v(10.1, 25.03) * mm, "end": v(9.92, 25.18) * mm});
            skArc(sketch, "E58.28.7", {"start": v(10.33, 23.2) * mm, "mid": v(10.32, 24.01) * mm, "end": v(10.2, 24.82) * mm});
            skLineSegment(sketch, "E58.28.8", {"start": v(10.33, 23.2) * mm, "end": v(9.81, 22.04) * mm});
            skArc(sketch, "E58.28.9", {"start": v(9.81, 22.04) * mm, "mid": v(9.8, 21.66) * mm, "end": v(10.06, 21.37) * mm});
            skArc(sketch, "E58.29.0", {"start": v(1.97, 23.54) * mm, "mid": v(2.34, 23.65) * mm, "end": v(2.52, 24) * mm});
            skLineSegment(sketch, "E58.29.1", {"start": v(2.66, 25.26) * mm, "end": v(2.52, 24) * mm});
            skArc(sketch, "E58.29.2", {"start": v(2.66, 25.26) * mm, "mid": v(3.07, 25.96) * mm, "end": v(3.57, 26.6) * mm});
            skArc(sketch, "E58.29.3", {"start": v(4, 26.76) * mm, "mid": v(3.76, 26.73) * mm, "end": v(3.57, 26.6) * mm});
            skLineSegment(sketch, "E58.29.4", {"start": v(4, 26.76) * mm, "end": v(4.24, 26.74) * mm});
            skLineSegment(sketch, "E58.29.5", {"start": v(4.47, 26.69) * mm, "end": v(4.24, 26.74) * mm});
            skArc(sketch, "E58.29.6", {"start": v(4.83, 26.4) * mm, "mid": v(4.68, 26.59) * mm, "end": v(4.47, 26.69) * mm});
            skArc(sketch, "E58.29.7", {"start": v(5.28, 24.84) * mm, "mid": v(5.1, 25.64) * mm, "end": v(4.83, 26.4) * mm});
            skLineSegment(sketch, "E58.29.8", {"start": v(5.28, 24.84) * mm, "end": v(5.02, 23.6) * mm});
            skArc(sketch, "E58.29.9", {"start": v(5.02, 23.6) * mm, "mid": v(5.08, 23.22) * mm, "end": v(5.4, 23) * mm});
            skArc(sketch, "E59.trimOffspring", {"start": v(-7.77, 22.3) * mm, "mid": v(-8.47, 22.05) * mm, "end": v(-9.15, 21.78) * mm});
            skArc(sketch, "E60.trimOffspring", {"start": v(-12.24, 20.2) * mm, "mid": v(-12.87, 19.81) * mm, "end": v(-13.48, 19.4) * mm});
            skArc(sketch, "E61.trimOffspring", {"start": v(-16.17, 17.22) * mm, "mid": v(-16.7, 16.7) * mm, "end": v(-17.22, 16.17) * mm});
            skArc(sketch, "E62.trimOffspring", {"start": v(-21.78, 9.15) * mm, "mid": v(-22.05, 8.47) * mm, "end": v(-22.3, 7.77) * mm});
            skArc(sketch, "E63.trimOffspring", {"start": v(-19.4, 13.48) * mm, "mid": v(-19.81, 12.87) * mm, "end": v(-20.2, 12.24) * mm});
            skArc(sketch, "E64.trimOffspring", {"start": v(-23.2, 4.42) * mm, "mid": v(-23.33, 3.7) * mm, "end": v(-23.44, 2.96) * mm});
            skArc(sketch, "E65.trimOffspring", {"start": v(-23.62, -0.5) * mm, "mid": v(-23.59, -1.24) * mm, "end": v(-23.54, -1.97) * mm});
            skArc(sketch, "E66.trimOffspring", {"start": v(-23, -5.4) * mm, "mid": v(-22.82, -6.11) * mm, "end": v(-22.61, -6.83) * mm});
            skArc(sketch, "E67.trimOffspring", {"start": v(-21.37, -10.06) * mm, "mid": v(-21.05, -10.72) * mm, "end": v(-20.7, -11.38) * mm});
            skArc(sketch, "E68.trimOffspring", {"start": v(-18.81, -14.28) * mm, "mid": v(-18.36, -14.87) * mm, "end": v(-17.88, -15.43) * mm});
            skArc(sketch, "E69.trimOffspring", {"start": v(-15.43, -17.88) * mm, "mid": v(-14.87, -18.36) * mm, "end": v(-14.28, -18.81) * mm});
            skArc(sketch, "E70.trimOffspring", {"start": v(-11.38, -20.7) * mm, "mid": v(-10.72, -21.05) * mm, "end": v(-10.06, -21.37) * mm});
            skArc(sketch, "E71.trimOffspring", {"start": v(-6.83, -22.61) * mm, "mid": v(-6.11, -22.82) * mm, "end": v(-5.4, -23) * mm});
            skArc(sketch, "E72.trimOffspring", {"start": v(-1.97, -23.54) * mm, "mid": v(-1.24, -23.59) * mm, "end": v(-0.5, -23.62) * mm});
            skArc(sketch, "E73.trimOffspring", {"start": v(1.97, 23.54) * mm, "mid": v(1.24, 23.59) * mm, "end": v(0.5, 23.62) * mm});
            skArc(sketch, "E74.trimOffspring", {"start": v(6.83, 22.61) * mm, "mid": v(6.11, 22.82) * mm, "end": v(5.4, 23) * mm});
            skArc(sketch, "E75.trimOffspring", {"start": v(11.38, 20.7) * mm, "mid": v(10.72, 21.05) * mm, "end": v(10.06, 21.37) * mm});
            skArc(sketch, "E76.trimOffspring", {"start": v(15.43, 17.88) * mm, "mid": v(14.87, 18.36) * mm, "end": v(14.28, 18.81) * mm});
            skArc(sketch, "E77.trimOffspring", {"start": v(18.81, 14.28) * mm, "mid": v(18.36, 14.87) * mm, "end": v(17.88, 15.43) * mm});
            skArc(sketch, "E78.trimOffspring", {"start": v(21.37, 10.06) * mm, "mid": v(21.05, 10.72) * mm, "end": v(20.7, 11.38) * mm});
            skArc(sketch, "E79.trimOffspring", {"start": v(23, 5.4) * mm, "mid": v(22.82, 6.11) * mm, "end": v(22.61, 6.83) * mm});
            skArc(sketch, "E80.trimOffspring", {"start": v(23.62, 0.5) * mm, "mid": v(23.59, 1.24) * mm, "end": v(23.54, 1.97) * mm});
            skArc(sketch, "E81.trimOffspring", {"start": v(23.2, -4.42) * mm, "mid": v(23.33, -3.7) * mm, "end": v(23.44, -2.96) * mm});
            skArc(sketch, "E82.trimOffspring", {"start": v(21.78, -9.15) * mm, "mid": v(22.05, -8.47) * mm, "end": v(22.3, -7.77) * mm});
            skArc(sketch, "E83.trimOffspring", {"start": v(19.4, -13.48) * mm, "mid": v(19.81, -12.87) * mm, "end": v(20.2, -12.24) * mm});
            skArc(sketch, "E84.trimOffspring", {"start": v(16.17, -17.22) * mm, "mid": v(16.7, -16.7) * mm, "end": v(17.22, -16.17) * mm});
            skArc(sketch, "E85.trimOffspring", {"start": v(12.24, -20.2) * mm, "mid": v(12.87, -19.81) * mm, "end": v(13.48, -19.4) * mm});
            skArc(sketch, "E86.trimOffspring", {"start": v(7.77, -22.3) * mm, "mid": v(8.47, -22.05) * mm, "end": v(9.15, -21.78) * mm});
            skArc(sketch, "E87.trimOffspring", {"start": v(2.96, -23.44) * mm, "mid": v(3.7, -23.33) * mm, "end": v(4.42, -23.2) * mm});
            skSolve(sketch);
        }
        {
            var Q0;
            Q0=makeQuery(id+"F0.imprint","IMPRINT",FACE,{"disambiguationData":[TD([[makeQuery(id+"F0.imprint","IMPRINT",EDGE,{"derivedFrom":sQuery(id+"F0.wireOp",EDGE,"E0")}),1.0]])]});
            var Q1;
            Q1=makeQuery(id+"F2.imprint","IMPRINT",FACE,{"disambiguationData":[TD([[makeQuery(id+"F2.imprint","IMPRINT",EDGE,{"derivedFrom":sQuery(id+"F2.wireOp",EDGE,"E44")}),1.0]])]});
            var Q2;
            Q2=sQuery(id+"F0.wireOp",VERTEX,"E5.MirrorCS.start");
            var Q3;
            Q3=sQuery(id+"F2.wireOp",VERTEX,"E58.28.4.start");
            loft(context, id + "F3", {"sheetProfilesArray" : [{ "sheetProfileEntities" : qUnion([Q0]) }, { "sheetProfileEntities" : qUnion([Q1]) }], "matchConnections" : true, "connections" : [{ "connectionEntities" : qUnion([Q2, Q3]), "connectionEdgeQueries" : qUnion([]), "connectionEdgeParameters" : [] }]});
        }
        {
            var Q0;
            Q0=makeQuery(id+"F3.opLoft","CAP_FACE",FACE,{"disambiguationData":[OSD([makeQuery(id+"F2.imprint","IMPRINT",FACE,{"disambiguationData":[TD([[makeQuery(id+"F2.imprint","IMPRINT",EDGE,{"derivedFrom":sQuery(id+"F2.wireOp",EDGE,"E44")}),1.0]])]})])],"isStart":true});
            var sketch = newSketch(context, id + "F4", { "sketchPlane" : qUnion([Q0])});
            skCircle(sketch, "E88", {"center": v(0, 0) * mm, "radius": 6.35 * mm});
            skSolve(sketch);
        }
        {
            var Q0;
            Q0 = qSketchRegion(id + "F4", true);
            extrude(context, id + "F5", {"entities" : qUnion([Q0]), "operationType" : NewBodyOperationType.REMOVE, "endBound" : BoundingType.THROUGH_ALL, "oppositeDirection" : true, "depth" : 25.4 * mm});
        }
    });
